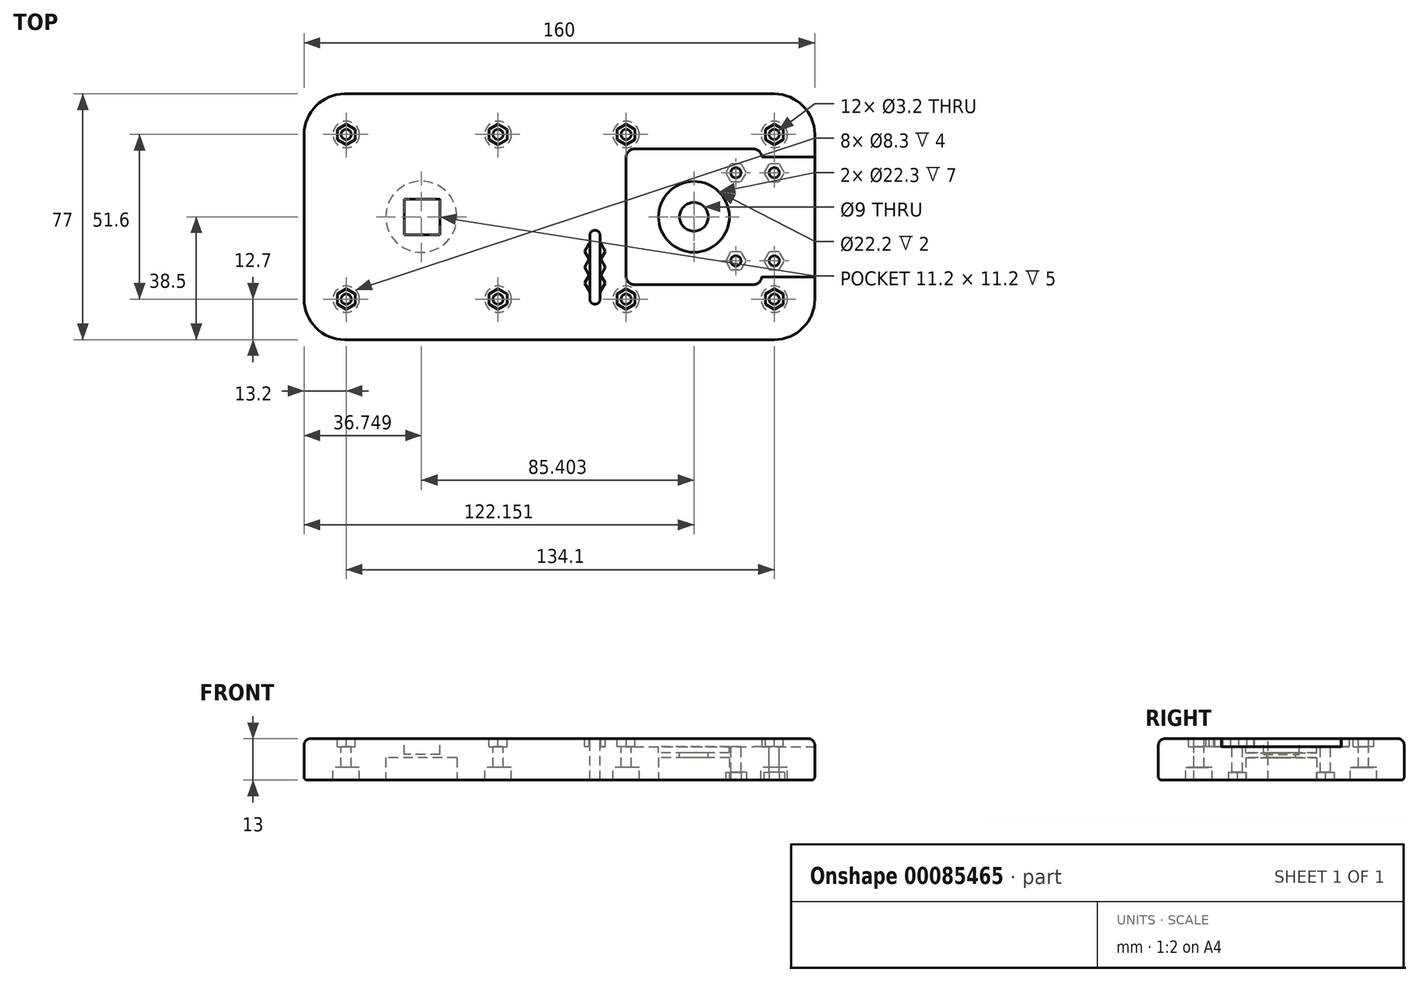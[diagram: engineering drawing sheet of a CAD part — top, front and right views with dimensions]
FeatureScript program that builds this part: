
annotation { "Feature Type Name" : "Feature", "Feature Type Description" : "" }
export const myFeature = defineFeature(function(context is Context, id is Id, definition is map)
    precondition{}
    {
        {
            var Q0;
            Q0=qCreatedBy(makeId("Top.planeOp"),FACE);
            var sketch = newSketch(context, id + "F0", { "sketchPlane" : qUnion([Q0])});
            skLineSegment(sketch, "E0.bottom", {"start": v(-147.3, 0) * mm, "end": v(-12.7, 0) * mm});
            skLineSegment(sketch, "E0.top", {"start": v(-147.3, 77) * mm, "end": v(-12.7, 77) * mm});
            skLineSegment(sketch, "E0.left", {"start": v(-160, 12.7) * mm, "end": v(-160, 64.3) * mm});
            skLineSegment(sketch, "E0.right", {"start": v(0, 12.7) * mm, "end": v(0, 64.3) * mm});
            skPoint(sketch, "E1.visualSharp", {"position": v(-160, 77) * mm});
            skArc(sketch, "E1.filletArc", {"start": v(-147.3, 77) * mm, "mid": v(-156.28, 73.28) * mm, "end": v(-160, 64.3) * mm});
            skPoint(sketch, "E2.visualSharp", {"position": v(0, 77) * mm});
            skArc(sketch, "E2.filletArc", {"start": v(0, 64.3) * mm, "mid": v(-3.72, 73.28) * mm, "end": v(-12.7, 77) * mm});
            skPoint(sketch, "E3.visualSharp", {"position": v(0, 0) * mm});
            skArc(sketch, "E3.filletArc", {"start": v(-12.7, 0) * mm, "mid": v(-3.72, 3.72) * mm, "end": v(0, 12.7) * mm});
            skPoint(sketch, "E4.visualSharp", {"position": v(-160, 0) * mm});
            skArc(sketch, "E4.filletArc", {"start": v(-160, 12.7) * mm, "mid": v(-156.28, 3.72) * mm, "end": v(-147.3, 0) * mm});
            skLineSegment(sketch, "E5.bottom", {"start": v(-56.56, 59.75) * mm, "end": v(-19.14, 59.75) * mm});
            skLineSegment(sketch, "E5.top", {"start": v(-56.56, 17.25) * mm, "end": v(-19.14, 17.25) * mm});
            skLineSegment(sketch, "E5.left", {"start": v(-59.1, 57.2) * mm, "end": v(-59.1, 19.79) * mm});
            skLineSegment(sketch, "E5.right", {"start": v(-16.6, 57.2) * mm, "end": v(-16.6, 19.79) * mm});
            skPoint(sketch, "E6.visualSharp", {"position": v(-59.1, 59.75) * mm});
            skArc(sketch, "E6.filletArc", {"start": v(-56.56, 59.75) * mm, "mid": v(-58.35, 59) * mm, "end": v(-59.1, 57.2) * mm});
            skPoint(sketch, "E7.visualSharp", {"position": v(-59.1, 17.25) * mm});
            skArc(sketch, "E7.filletArc", {"start": v(-59.1, 19.79) * mm, "mid": v(-58.35, 18) * mm, "end": v(-56.56, 17.25) * mm});
            skPoint(sketch, "E8.visualSharp", {"position": v(-16.6, 17.25) * mm});
            skArc(sketch, "E8.filletArc", {"start": v(-19.14, 17.25) * mm, "mid": v(-17.34, 18) * mm, "end": v(-16.6, 19.79) * mm});
            skPoint(sketch, "E9.visualSharp", {"position": v(-16.6, 59.75) * mm});
            skArc(sketch, "E9.filletArc", {"start": v(-16.6, 57.2) * mm, "mid": v(-17.34, 59) * mm, "end": v(-19.14, 59.75) * mm});
            skSolve(sketch);
        }
        {
            var Q0;
            Q0=makeQuery(id+"F0.imprint","IMPRINT",FACE,{"disambiguationData":[TD([[makeQuery(id+"F0.imprint","IMPRINT",EDGE,{"derivedFrom":sQuery(id+"F0.wireOp",EDGE,"E0.bottom")}),1.0]])]});
            extrude(context, id + "F1", {"entities" : qUnion([Q0]), "depth" : 13 * mm});
        }
        {
            var Q0;
            Q0=makeQuery(id+"F0.imprint","IMPRINT",FACE,{"disambiguationData":[TD([[makeQuery(id+"F0.imprint","IMPRINT",EDGE,{"derivedFrom":sQuery(id+"F0.wireOp",EDGE,"E5.bottom")}),-1.0]])]});
            extrude(context, id + "F2", {"entities" : qUnion([Q0]), "operationType" : NewBodyOperationType.ADD, "depth" : 10.5 * mm});
        }
        {
            var Q0;
            Q0=makeQuery(id+"F1.opExtrude","CAP_FACE",FACE,{"disambiguationData":[OSD([sQuery(id+"F0.wireOp",EDGE,"E0.bottom"),sQuery(id+"F0.wireOp",EDGE,"E0.top"),sQuery(id+"F0.wireOp",EDGE,"E0.left"),sQuery(id+"F0.wireOp",EDGE,"E0.right"),sQuery(id+"F0.wireOp",EDGE,"E1.filletArc"),sQuery(id+"F0.wireOp",EDGE,"E2.filletArc"),sQuery(id+"F0.wireOp",EDGE,"E3.filletArc"),sQuery(id+"F0.wireOp",EDGE,"E4.filletArc"),sQuery(id+"F0.wireOp",EDGE,"E5.bottom"),sQuery(id+"F0.wireOp",EDGE,"E5.top"),sQuery(id+"F0.wireOp",EDGE,"E5.left"),sQuery(id+"F0.wireOp",EDGE,"E5.right"),sQuery(id+"F0.wireOp",EDGE,"E6.filletArc"),sQuery(id+"F0.wireOp",EDGE,"E7.filletArc"),sQuery(id+"F0.wireOp",EDGE,"E8.filletArc"),sQuery(id+"F0.wireOp",EDGE,"E9.filletArc")])],"isStart":false});
            var sketch = newSketch(context, id + "F3", { "sketchPlane" : qUnion([Q0])});
            skLineSegment(sketch, "E10.right", {"start": v(-12.7, 64.3) * mm, "end": v(-12.7, 12.7) * mm, "construction": true});
            skCircle(sketch, "E11", {"center": v(-146.8, 64.3) * mm, "radius": 1.6 * mm});
            skCircle(sketch, "E12", {"center": v(-146.8, 12.7) * mm, "radius": 1.6 * mm});
            skCircle(sketch, "E13", {"center": v(-12.7, 12.7) * mm, "radius": 1.6 * mm});
            skCircle(sketch, "E14", {"center": v(-12.7, 64.3) * mm, "radius": 1.6 * mm});
            skCircle(sketch, "E15", {"center": v(-59.1, 12.7) * mm, "radius": 1.6 * mm});
            skCircle(sketch, "E16", {"center": v(-59.1, 64.3) * mm, "radius": 1.6 * mm});
            skCircle(sketch, "E17", {"center": v(-99.2, 64.3) * mm, "radius": 1.6 * mm});
            skCircle(sketch, "E18", {"center": v(-99.2, 12.7) * mm, "radius": 1.6 * mm});
            skCircle(sketch, "E19", {"center": v(-99.2, 64.3) * mm, "radius": 3 * mm});
            skCircle(sketch, "E20", {"center": v(-146.8, 64.3) * mm, "radius": 3 * mm});
            skCircle(sketch, "E21", {"center": v(-146.8, 12.7) * mm, "radius": 3 * mm});
            skCircle(sketch, "E22", {"center": v(-99.2, 12.7) * mm, "radius": 3 * mm});
            skLineSegment(sketch, "E23", {"start": v(-146.8, 12.7) * mm, "end": v(-12.7, 12.7) * mm, "construction": true});
            skLineSegment(sketch, "E24", {"start": v(-146.8, 64.3) * mm, "end": v(-12.7, 64.3) * mm, "construction": true});
            skLineSegment(sketch, "E25", {"start": v(-99.2, 64.3) * mm, "end": v(-99.2, 12.7) * mm, "construction": true});
            skLineSegment(sketch, "E26", {"start": v(-146.8, 12.7) * mm, "end": v(-146.8, 64.3) * mm, "construction": true});
            skLineSegment(sketch, "E27", {"start": v(-99.2, 12.7) * mm, "end": v(-146.8, 64.3) * mm, "construction": true});
            skLineSegment(sketch, "E28", {"start": v(-146.8, 12.7) * mm, "end": v(-99.2, 64.3) * mm, "construction": true});
            skCircle(sketch, "E29", {"center": v(-12.7, 64.3) * mm, "radius": 4.15 * mm});
            skCircle(sketch, "E30", {"center": v(-12.7, 12.7) * mm, "radius": 4.15 * mm});
            skCircle(sketch, "E31", {"center": v(-59.1, 12.7) * mm, "radius": 4.15 * mm});
            skCircle(sketch, "E32", {"center": v(-59.1, 64.3) * mm, "radius": 4.15 * mm});
            skCircle(sketch, "E33", {"center": v(-99.2, 64.3) * mm, "radius": 4.15 * mm});
            skCircle(sketch, "E34", {"center": v(-99.2, 12.7) * mm, "radius": 4.15 * mm});
            skCircle(sketch, "E35", {"center": v(-146.8, 12.7) * mm, "radius": 4.15 * mm});
            skCircle(sketch, "E36", {"center": v(-146.8, 64.3) * mm, "radius": 4.15 * mm});
            skLineSegment(sketch, "E37", {"start": v(-12.7, 64.3) * mm, "end": v(-12.7, 52.3) * mm, "construction": true});
            skLineSegment(sketch, "E38", {"start": v(-12.7, 12.7) * mm, "end": v(-12.7, 24.7) * mm, "construction": true});
            skLineSegment(sketch, "E39", {"start": v(-12.7, 24.7) * mm, "end": v(-24.7, 24.7) * mm, "construction": true});
            skLineSegment(sketch, "E40", {"start": v(-12.7, 52.3) * mm, "end": v(-24.7, 52.3) * mm, "construction": true});
            skCircle(sketch, "E41", {"center": v(-24.7, 52.3) * mm, "radius": 1.6 * mm});
            skCircle(sketch, "E42", {"center": v(-12.7, 52.3) * mm, "radius": 1.6 * mm});
            skCircle(sketch, "E43", {"center": v(-12.7, 24.7) * mm, "radius": 1.6 * mm});
            skCircle(sketch, "E44", {"center": v(-24.7, 24.7) * mm, "radius": 1.6 * mm});
            skPoint(sketch, "E45", {"position": v(-143.99, 15.75) * mm});
            skPoint(sketch, "E46", {"position": v(-102.02, 61.25) * mm});
            skSolve(sketch);
        }
        {
            var Q0;
            Q0=makeQuery(id+"F3.imprint","IMPRINT",FACE,{"disambiguationData":[TD([[makeQuery(id+"F3.imprint","IMPRINT",EDGE,{"derivedFrom":sQuery(id+"F3.wireOp",EDGE,"E11")}),1.0]])]});
            var Q1;
            Q1=makeQuery(id+"F3.imprint","IMPRINT",FACE,{"disambiguationData":[TD([[makeQuery(id+"F3.imprint","IMPRINT",EDGE,{"derivedFrom":sQuery(id+"F3.wireOp",EDGE,"E12")}),1.0]])]});
            var Q2;
            Q2=makeQuery(id+"F3.imprint","IMPRINT",FACE,{"disambiguationData":[TD([[makeQuery(id+"F3.imprint","IMPRINT",EDGE,{"derivedFrom":sQuery(id+"F3.wireOp",EDGE,"E13")}),1.0]])]});
            var Q3;
            Q3=makeQuery(id+"F3.imprint","IMPRINT",FACE,{"disambiguationData":[TD([[makeQuery(id+"F3.imprint","IMPRINT",EDGE,{"derivedFrom":sQuery(id+"F3.wireOp",EDGE,"E14")}),1.0]])]});
            var Q4;
            Q4=makeQuery(id+"F3.imprint","IMPRINT",FACE,{"disambiguationData":[TD([[makeQuery(id+"F3.imprint","IMPRINT",EDGE,{"derivedFrom":sQuery(id+"F3.wireOp",EDGE,"E15")}),1.0]])]});
            var Q5;
            Q5=makeQuery(id+"F3.imprint","IMPRINT",FACE,{"disambiguationData":[TD([[makeQuery(id+"F3.imprint","IMPRINT",EDGE,{"derivedFrom":sQuery(id+"F3.wireOp",EDGE,"E16")}),1.0]])]});
            var Q6;
            Q6=makeQuery(id+"F3.imprint","IMPRINT",FACE,{"disambiguationData":[TD([[makeQuery(id+"F3.imprint","IMPRINT",EDGE,{"derivedFrom":sQuery(id+"F3.wireOp",EDGE,"E17")}),1.0]])]});
            var Q7;
            Q7=makeQuery(id+"F3.imprint","IMPRINT",FACE,{"disambiguationData":[TD([[makeQuery(id+"F3.imprint","IMPRINT",EDGE,{"derivedFrom":sQuery(id+"F3.wireOp",EDGE,"E18")}),1.0]])]});
            var Q8;
            Q8=makeQuery(id+"F3.imprint","IMPRINT",FACE,{"disambiguationData":[TD([[makeQuery(id+"F3.imprint","IMPRINT",EDGE,{"derivedFrom":sQuery(id+"F3.wireOp",EDGE,"E42")}),1.0]])]});
            var Q9;
            Q9=makeQuery(id+"F3.imprint","IMPRINT",FACE,{"disambiguationData":[TD([[makeQuery(id+"F3.imprint","IMPRINT",EDGE,{"derivedFrom":sQuery(id+"F3.wireOp",EDGE,"E43")}),1.0]])]});
            var Q10;
            Q10=makeQuery(id+"F3.imprint","IMPRINT",FACE,{"disambiguationData":[TD([[makeQuery(id+"F3.imprint","IMPRINT",EDGE,{"derivedFrom":sQuery(id+"F3.wireOp",EDGE,"E44")}),1.0]])]});
            var Q11;
            Q11=makeQuery(id+"F3.imprint","IMPRINT",FACE,{"disambiguationData":[TD([[makeQuery(id+"F3.imprint","IMPRINT",EDGE,{"derivedFrom":sQuery(id+"F3.wireOp",EDGE,"E41")}),1.0]])]});
            extrude(context, id + "F4", {"entities" : qUnion([Q0, Q1, Q2, Q3, Q4, Q5, Q6, Q7, Q8, Q9, Q10, Q11]), "operationType" : NewBodyOperationType.REMOVE, "endBound" : BoundingType.UP_TO_NEXT, "oppositeDirection" : true, "depth" : 29.76 * mm});
        }
        {
            var Q0;
            Q0=makeQuery(id+"F0.imprint","IMPRINT",FACE,{"disambiguationData":[TD([[makeQuery(id+"F0.imprint","IMPRINT",EDGE,{"derivedFrom":sQuery(id+"F0.wireOp",EDGE,"E5.bottom")}),-1.0]])]});
            var sketch = newSketch(context, id + "F5", { "sketchPlane" : qUnion([Q0])});
            skLineSegment(sketch, "E47.0.0", {"start": v(-19.14, 59.75) * mm, "end": v(-56.56, 59.75) * mm});
            skArc(sketch, "E47.0.1", {"start": v(-56.56, 59.75) * mm, "mid": v(-58.35, 59) * mm, "end": v(-59.1, 57.2) * mm});
            skLineSegment(sketch, "E47.0.2", {"start": v(-59.1, 57.2) * mm, "end": v(-59.1, 19.79) * mm, "construction": true});
            skArc(sketch, "E47.0.3", {"start": v(-59.1, 19.79) * mm, "mid": v(-58.35, 18) * mm, "end": v(-56.56, 17.25) * mm, "construction": true});
            skLineSegment(sketch, "E47.0.4", {"start": v(-56.56, 17.25) * mm, "end": v(-19.14, 17.25) * mm});
            skArc(sketch, "E47.0.5", {"start": v(-19.14, 17.25) * mm, "mid": v(-17.34, 18) * mm, "end": v(-16.6, 19.79) * mm, "construction": true});
            skLineSegment(sketch, "E47.0.6", {"start": v(-16.6, 19.79) * mm, "end": v(-16.6, 57.2) * mm});
            skArc(sketch, "E47.0.7", {"start": v(-16.6, 57.2) * mm, "mid": v(-17.34, 59) * mm, "end": v(-19.14, 59.75) * mm, "construction": true});
            skLineSegment(sketch, "E48", {"start": v(-19.14, 19.79) * mm, "end": v(-56.56, 57.21) * mm, "construction": true});
            skLineSegment(sketch, "E49", {"start": v(-56.56, 19.79) * mm, "end": v(-19.14, 57.2) * mm, "construction": true});
            skPoint(sketch, "E50", {"position": v(-37.85, 38.5) * mm});
            skCircle(sketch, "E51", {"center": v(-37.85, 38.5) * mm, "radius": 11.15 * mm});
            skSolve(sketch);
        }
        {
            var Q0;
            Q0=qSketchRegion(id+"F5",true);
            extrude(context, id + "F6", {"entities" : qUnion([Q0]), "operationType" : NewBodyOperationType.REMOVE, "depth" : 7 * mm});
        }
        {
            var Q0;
            Q0=makeQuery(id+"F2.opExtrude","CAP_FACE",FACE,{"disambiguationData":[OSD([sQuery(id+"F0.wireOp",EDGE,"E5.bottom"),sQuery(id+"F0.wireOp",EDGE,"E5.top"),sQuery(id+"F0.wireOp",EDGE,"E5.left"),sQuery(id+"F0.wireOp",EDGE,"E5.right"),sQuery(id+"F0.wireOp",EDGE,"E6.filletArc"),sQuery(id+"F0.wireOp",EDGE,"E7.filletArc"),sQuery(id+"F0.wireOp",EDGE,"E8.filletArc"),sQuery(id+"F0.wireOp",EDGE,"E9.filletArc")])],"isStart":false});
            var sketch = newSketch(context, id + "F7", { "sketchPlane" : qUnion([Q0])});
            skLineSegment(sketch, "E52", {"start": v(-56.56, 19.79) * mm, "end": v(-19.14, 57.2) * mm, "construction": true});
            skLineSegment(sketch, "E53", {"start": v(-56.56, 57.21) * mm, "end": v(-19.14, 19.79) * mm, "construction": true});
            skCircle(sketch, "E54", {"center": v(-37.85, 38.5) * mm, "radius": 4.5 * mm});
            skCircle(sketch, "E55", {"center": v(-37.85, 38.5) * mm, "radius": 11.1 * mm});
            skSolve(sketch);
        }
        {
            var Q0;
            Q0=makeQuery(id+"F7.imprint","IMPRINT",FACE,{"disambiguationData":[TD([[makeQuery(id+"F7.imprint","IMPRINT",EDGE,{"derivedFrom":sQuery(id+"F7.wireOp",EDGE,"E54")}),1.0]])]});
            var Q1;
            Q1=sQuery(id+"F7.wireOp",EDGE,"E54");
            extrude(context, id + "F8", {"entities" : qUnion([Q0]), "operationType" : NewBodyOperationType.REMOVE, "surfaceEntities" : qUnion([Q1]), "oppositeDirection" : true, "depth" : 9 * mm});
        }
        {
            var Q0;
            Q0=makeQuery(id+"F0.imprint","IMPRINT",FACE,{"disambiguationData":[TD([[makeQuery(id+"F0.imprint","IMPRINT",EDGE,{"derivedFrom":sQuery(id+"F0.wireOp",EDGE,"E0.bottom")}),1.0]])]});
            var sketch = newSketch(context, id + "F9", { "sketchPlane" : qUnion([Q0])});
            skPoint(sketch, "E56.0", {"position": v(-147.3, 64.3) * mm});
            skCircle(sketch, "E57.0", {"center": v(-146.8, 64.3) * mm, "radius": 1.6 * mm});
            skCircle(sketch, "E58.0", {"center": v(-99.2, 64.3) * mm, "radius": 1.6 * mm});
            skCircle(sketch, "E59.0", {"center": v(-99.2, 12.7) * mm, "radius": 1.6 * mm});
            skCircle(sketch, "E60.0", {"center": v(-146.8, 12.7) * mm, "radius": 1.6 * mm});
            skLineSegment(sketch, "E61", {"start": v(-146.8, 12.7) * mm, "end": v(-99.2, 64.3) * mm, "construction": true});
            skLineSegment(sketch, "E62", {"start": v(-99.2, 12.7) * mm, "end": v(-147.3, 64.3) * mm, "construction": true});
            skPoint(sketch, "E63.endSnap0", {"position": v(-123.25, 38.5) * mm});
            skCircle(sketch, "E64.0", {"center": v(-59.1, 64.3) * mm, "radius": 1.6 * mm});
            skCircle(sketch, "E65.0", {"center": v(-12.7, 12.7) * mm, "radius": 1.6 * mm});
            skCircle(sketch, "E66.0", {"center": v(-12.7, 64.3) * mm, "radius": 1.6 * mm});
            skCircle(sketch, "E67.0", {"center": v(-59.1, 12.7) * mm, "radius": 1.6 * mm});
            skCircle(sketch, "E68.0", {"center": v(-37.85, 38.5) * mm, "radius": 4.5 * mm});
            skLineSegment(sketch, "E69", {"start": v(-123.25, 38.5) * mm, "end": v(-37.85, 38.5) * mm, "construction": true});
            skCircle(sketch, "E70", {"center": v(-123.25, 38.5) * mm, "radius": 11.15 * mm});
            skLineSegment(sketch, "E71", {"start": v(-146.8, 12.7) * mm, "end": v(-99.2, 12.7) * mm, "construction": true});
            skLineSegment(sketch, "E72", {"start": v(-59.1, 12.7) * mm, "end": v(-12.7, 12.7) * mm, "construction": true});
            skLineSegment(sketch, "E73", {"start": v(-123.25, 38.5) * mm, "end": v(-123.25, 12.7) * mm, "construction": true});
            skLineSegment(sketch, "E74", {"start": v(-37.85, 38.5) * mm, "end": v(-37.85, 12.7) * mm, "construction": true});
            skLineSegment(sketch, "E75", {"start": v(-123.25, 27.35) * mm, "end": v(-37.85, 27.35) * mm, "construction": true});
            skLineSegment(sketch, "E76.bottom", {"start": v(-67.85, 12.7) * mm, "end": v(-69.85, 12.7) * mm});
            skLineSegment(sketch, "E77", {"start": v(-68.85, 12.7) * mm, "end": v(-68.85, 17.7) * mm, "construction": true});
            skLineSegment(sketch, "E78", {"start": v(-68.85, 17.7) * mm, "end": v(-68.85, 22.7) * mm, "construction": true});
            skLineSegment(sketch, "E79", {"start": v(-68.85, 22.7) * mm, "end": v(-68.85, 27.7) * mm, "construction": true});
            skLineSegment(sketch, "E80", {"start": v(-68.85, 27.7) * mm, "end": v(-68.85, 32.7) * mm, "construction": true});
            skLineSegment(sketch, "E81", {"start": v(-69.85, 12.7) * mm, "end": v(-69.85, 32.7) * mm});
            skLineSegment(sketch, "E82", {"start": v(-69.85, 32.7) * mm, "end": v(-67.85, 32.7) * mm});
            skLineSegment(sketch, "E83", {"start": v(-67.85, 32.7) * mm, "end": v(-67.85, 12.7) * mm});
            skLineSegment(sketch, "E84", {"start": v(-37.85, 24.21) * mm, "end": v(-68.85, 24.21) * mm, "construction": true});
            skLineSegment(sketch, "E85", {"start": v(-68.52, 38.5) * mm, "end": v(-68.52, 32.7) * mm, "construction": true});
            skLineSegment(sketch, "E86", {"start": v(-59.1, 12.7) * mm, "end": v(-99.2, 12.7) * mm, "construction": true});
            skCircle(sketch, "E87.cCircle", {"center": v(-68.85, 32.7) * mm, "radius": 3.23 * mm, "construction": true});
            skLineSegment(sketch, "E87.0", {"start": v(-65.62, 32.7) * mm, "end": v(-67.23, 29.9) * mm});
            skLineSegment(sketch, "E87.1", {"start": v(-67.23, 29.9) * mm, "end": v(-70.47, 29.9) * mm});
            skLineSegment(sketch, "E87.2", {"start": v(-70.47, 29.9) * mm, "end": v(-72.08, 32.7) * mm});
            skLineSegment(sketch, "E87.3", {"start": v(-72.08, 32.7) * mm, "end": v(-70.47, 35.5) * mm});
            skLineSegment(sketch, "E87.4", {"start": v(-70.47, 35.5) * mm, "end": v(-67.23, 35.5) * mm});
            skLineSegment(sketch, "E87.5", {"start": v(-67.23, 35.5) * mm, "end": v(-65.62, 32.7) * mm});
            skCircle(sketch, "E88.cCircle", {"center": v(-68.85, 27.7) * mm, "radius": 3.23 * mm, "construction": true});
            skLineSegment(sketch, "E88.0", {"start": v(-65.62, 27.7) * mm, "end": v(-67.23, 24.9) * mm});
            skLineSegment(sketch, "E88.1", {"start": v(-67.23, 24.9) * mm, "end": v(-70.47, 24.9) * mm});
            skLineSegment(sketch, "E88.2", {"start": v(-70.47, 24.9) * mm, "end": v(-72.08, 27.7) * mm});
            skLineSegment(sketch, "E88.3", {"start": v(-72.08, 27.7) * mm, "end": v(-70.47, 30.5) * mm});
            skLineSegment(sketch, "E88.4", {"start": v(-70.47, 30.5) * mm, "end": v(-67.23, 30.5) * mm});
            skLineSegment(sketch, "E88.5", {"start": v(-67.23, 30.5) * mm, "end": v(-65.62, 27.7) * mm});
            skCircle(sketch, "E89.cCircle", {"center": v(-68.85, 22.7) * mm, "radius": 3.23 * mm, "construction": true});
            skLineSegment(sketch, "E89.0", {"start": v(-65.62, 22.7) * mm, "end": v(-67.23, 19.9) * mm});
            skLineSegment(sketch, "E89.1", {"start": v(-67.23, 19.9) * mm, "end": v(-70.47, 19.9) * mm});
            skLineSegment(sketch, "E89.2", {"start": v(-70.47, 19.9) * mm, "end": v(-72.08, 22.7) * mm});
            skLineSegment(sketch, "E89.3", {"start": v(-72.08, 22.7) * mm, "end": v(-70.47, 25.5) * mm});
            skLineSegment(sketch, "E89.4", {"start": v(-70.47, 25.5) * mm, "end": v(-67.23, 25.5) * mm});
            skLineSegment(sketch, "E89.5", {"start": v(-67.23, 25.5) * mm, "end": v(-65.62, 22.7) * mm});
            skCircle(sketch, "E90.cCircle", {"center": v(-68.85, 17.7) * mm, "radius": 3.23 * mm, "construction": true});
            skLineSegment(sketch, "E90.0", {"start": v(-65.62, 17.7) * mm, "end": v(-67.23, 14.9) * mm});
            skLineSegment(sketch, "E90.1", {"start": v(-67.23, 14.9) * mm, "end": v(-70.47, 14.9) * mm});
            skLineSegment(sketch, "E90.2", {"start": v(-70.47, 14.9) * mm, "end": v(-72.08, 17.7) * mm});
            skLineSegment(sketch, "E90.3", {"start": v(-72.08, 17.7) * mm, "end": v(-70.47, 20.5) * mm});
            skLineSegment(sketch, "E90.4", {"start": v(-70.47, 20.5) * mm, "end": v(-67.23, 20.5) * mm});
            skLineSegment(sketch, "E90.5", {"start": v(-67.23, 20.5) * mm, "end": v(-65.62, 17.7) * mm});
            skCircle(sketch, "E91.cCircle", {"center": v(-68.85, 12.7) * mm, "radius": 3.23 * mm, "construction": true});
            skLineSegment(sketch, "E91.0", {"start": v(-65.62, 12.7) * mm, "end": v(-67.23, 9.9) * mm});
            skLineSegment(sketch, "E91.1", {"start": v(-67.23, 9.9) * mm, "end": v(-70.47, 9.9) * mm});
            skLineSegment(sketch, "E91.2", {"start": v(-70.47, 9.9) * mm, "end": v(-72.08, 12.7) * mm});
            skLineSegment(sketch, "E91.3", {"start": v(-72.08, 12.7) * mm, "end": v(-70.47, 15.5) * mm});
            skLineSegment(sketch, "E91.4", {"start": v(-70.47, 15.5) * mm, "end": v(-67.23, 15.5) * mm});
            skLineSegment(sketch, "E91.5", {"start": v(-67.23, 15.5) * mm, "end": v(-65.62, 12.7) * mm});
            skSolve(sketch);
        }
        {
            var Q0;
            Q0=makeQuery(id+"F9.imprint","IMPRINT",FACE,{"disambiguationData":[TD([[makeQuery(id+"F9.imprint","IMPRINT",EDGE,{"derivedFrom":sQuery(id+"F9.wireOp",EDGE,"E70")}),1.0]])]});
            extrude(context, id + "F10", {"entities" : qUnion([Q0]), "operationType" : NewBodyOperationType.REMOVE, "depth" : 7 * mm});
        }
        {
            var Q0;
            Q0=makeQuery(id+"F3.imprint","IMPRINT",FACE,{"disambiguationData":[TD([[makeQuery(id+"F3.imprint","IMPRINT",EDGE,{"derivedFrom":sQuery(id+"F3.wireOp",EDGE,"E13")}),-1.0]])]});
            var Q1;
            Q1=makeQuery(id+"F3.imprint","IMPRINT",FACE,{"disambiguationData":[TD([[makeQuery(id+"F3.imprint","IMPRINT",EDGE,{"derivedFrom":sQuery(id+"F3.wireOp",EDGE,"E15")}),-1.0]])]});
            var Q2;
            Q2=makeQuery(id+"F3.imprint","IMPRINT",FACE,{"disambiguationData":[TD([[makeQuery(id+"F3.imprint","IMPRINT",EDGE,{"derivedFrom":sQuery(id+"F3.wireOp",EDGE,"E14")}),-1.0]])]});
            var Q3;
            Q3=makeQuery(id+"F3.imprint","IMPRINT",FACE,{"disambiguationData":[TD([[makeQuery(id+"F3.imprint","IMPRINT",EDGE,{"derivedFrom":sQuery(id+"F3.wireOp",EDGE,"E16")}),-1.0]])]});
            var Q4;
            Q4=makeQuery(id+"F3.imprint","IMPRINT",FACE,{"disambiguationData":[TD([[makeQuery(id+"F3.imprint","IMPRINT",EDGE,{"derivedFrom":sQuery(id+"F3.wireOp",EDGE,"E18")}),-1.0]])]});
            var Q5;
            Q5=makeQuery(id+"F3.imprint","IMPRINT",FACE,{"disambiguationData":[TD([[makeQuery(id+"F3.imprint","IMPRINT",EDGE,{"derivedFrom":sQuery(id+"F3.wireOp",EDGE,"E17")}),-1.0]])]});
            var Q6;
            Q6=makeQuery(id+"F3.imprint","IMPRINT",FACE,{"disambiguationData":[TD([[makeQuery(id+"F3.imprint","IMPRINT",EDGE,{"derivedFrom":sQuery(id+"F3.wireOp",EDGE,"E11")}),-1.0]])]});
            var Q7;
            Q7=makeQuery(id+"F3.imprint","IMPRINT",FACE,{"disambiguationData":[TD([[makeQuery(id+"F3.imprint","IMPRINT",EDGE,{"derivedFrom":sQuery(id+"F3.wireOp",EDGE,"E12")}),-1.0]])]});
            var Q8;
            {var subQ0=sQuery(id+"F3.wireOp",EDGE,"Ve5UWHnS-peIv-7Eyy-3Cd5-ivY1OEfJHqwA.left");var subQ1=sQuery(id+"F3.wireOp",EDGE,"Ve5UWHnS-peIv-7Eyy-3Cd5-ivY1OEfJHqwA.top");var subQ2=makeQuery(id+"F3.imprint","INTERSECT",VERTEX,{"derivedFrom":[subQ1,subQ0]});Q8=makeQuery(id+"F3.imprint","IMPRINT",FACE,{"disambiguationData":[TD([[makeQuery(id+"F3.imprint","IMPRINT",EDGE,{"disambiguationData":[TD([[subQ2,-1.0]])],"derivedFrom":subQ1}),1.0]])]});}
            var Q9;
            {var subQ0=sQuery(id+"F3.wireOp",EDGE,"Ve5UWHnS-peIv-7Eyy-3Cd5-ivY1OEfJHqwA.left");var subQ1=sQuery(id+"F3.wireOp",EDGE,"Ve5UWHnS-peIv-7Eyy-3Cd5-ivY1OEfJHqwA.bottom");var subQ2=makeQuery(id+"F3.imprint","INTERSECT",VERTEX,{"derivedFrom":[subQ1,subQ0]});Q9=makeQuery(id+"F3.imprint","IMPRINT",FACE,{"disambiguationData":[TD([[makeQuery(id+"F3.imprint","IMPRINT",EDGE,{"disambiguationData":[TD([[subQ2,-1.0]])],"derivedFrom":subQ1}),-1.0]])]});}
            var Q10;
            {var subQ0=sQuery(id+"F3.wireOp",EDGE,"qpdfHU9s-RBNK-oNWM-wD5O-6DZd83lqHaN6.left");var subQ1=sQuery(id+"F3.wireOp",EDGE,"qpdfHU9s-RBNK-oNWM-wD5O-6DZd83lqHaN6.top");var subQ2=makeQuery(id+"F3.imprint","INTERSECT",VERTEX,{"derivedFrom":[subQ1,subQ0]});Q10=makeQuery(id+"F3.imprint","IMPRINT",FACE,{"disambiguationData":[TD([[makeQuery(id+"F3.imprint","IMPRINT",EDGE,{"disambiguationData":[TD([[subQ2,-1.0]])],"derivedFrom":subQ1}),-1.0]])]});}
            var Q11;
            {var subQ0=sQuery(id+"F3.wireOp",EDGE,"qpdfHU9s-RBNK-oNWM-wD5O-6DZd83lqHaN6.right");var subQ1=sQuery(id+"F3.wireOp",EDGE,"qpdfHU9s-RBNK-oNWM-wD5O-6DZd83lqHaN6.top");var subQ2=makeQuery(id+"F3.imprint","INTERSECT",VERTEX,{"derivedFrom":[subQ1,subQ0]});Q11=makeQuery(id+"F3.imprint","IMPRINT",FACE,{"disambiguationData":[TD([[makeQuery(id+"F3.imprint","IMPRINT",EDGE,{"disambiguationData":[TD([[subQ2,1.0]])],"derivedFrom":subQ1}),-1.0]])]});}
            var Q12;
            {var subQ0=sQuery(id+"F3.wireOp",EDGE,"qpdfHU9s-RBNK-oNWM-wD5O-6DZd83lqHaN6.right");var subQ1=sQuery(id+"F3.wireOp",EDGE,"qpdfHU9s-RBNK-oNWM-wD5O-6DZd83lqHaN6.bottom");var subQ2=makeQuery(id+"F3.imprint","INTERSECT",VERTEX,{"derivedFrom":[subQ1,subQ0]});Q12=makeQuery(id+"F3.imprint","IMPRINT",FACE,{"disambiguationData":[TD([[makeQuery(id+"F3.imprint","IMPRINT",EDGE,{"disambiguationData":[TD([[subQ2,1.0]])],"derivedFrom":subQ1}),1.0]])]});}
            var Q13;
            {var subQ0=sQuery(id+"F3.wireOp",EDGE,"qpdfHU9s-RBNK-oNWM-wD5O-6DZd83lqHaN6.left");var subQ1=sQuery(id+"F3.wireOp",EDGE,"qpdfHU9s-RBNK-oNWM-wD5O-6DZd83lqHaN6.bottom");var subQ2=makeQuery(id+"F3.imprint","INTERSECT",VERTEX,{"derivedFrom":[subQ1,subQ0]});Q13=makeQuery(id+"F3.imprint","IMPRINT",FACE,{"disambiguationData":[TD([[makeQuery(id+"F3.imprint","IMPRINT",EDGE,{"disambiguationData":[TD([[subQ2,-1.0]])],"derivedFrom":subQ1}),1.0]])]});}
            var Q14;
            {var subQ0=sQuery(id+"F3.wireOp",EDGE,"Ve5UWHnS-peIv-7Eyy-3Cd5-ivY1OEfJHqwA.right");var subQ1=sQuery(id+"F3.wireOp",EDGE,"Ve5UWHnS-peIv-7Eyy-3Cd5-ivY1OEfJHqwA.top");var subQ2=makeQuery(id+"F3.imprint","INTERSECT",VERTEX,{"derivedFrom":[subQ1,subQ0]});Q14=makeQuery(id+"F3.imprint","IMPRINT",FACE,{"disambiguationData":[TD([[makeQuery(id+"F3.imprint","IMPRINT",EDGE,{"disambiguationData":[TD([[subQ2,1.0]])],"derivedFrom":subQ1}),1.0]])]});}
            var Q15;
            {var subQ0=sQuery(id+"F3.wireOp",EDGE,"Ve5UWHnS-peIv-7Eyy-3Cd5-ivY1OEfJHqwA.right");var subQ1=sQuery(id+"F3.wireOp",EDGE,"Ve5UWHnS-peIv-7Eyy-3Cd5-ivY1OEfJHqwA.bottom");var subQ2=makeQuery(id+"F3.imprint","INTERSECT",VERTEX,{"derivedFrom":[subQ1,subQ0]});Q15=makeQuery(id+"F3.imprint","IMPRINT",FACE,{"disambiguationData":[TD([[makeQuery(id+"F3.imprint","IMPRINT",EDGE,{"disambiguationData":[TD([[subQ2,1.0]])],"derivedFrom":subQ1}),-1.0]])]});}
            var Q16;
            {var subQ0=sQuery(id+"F3.wireOp",EDGE,"M7g3rWNN-r2re-sdfs-xWe1-7BCIrnAAYx4U.left");var subQ1=sQuery(id+"F3.wireOp",EDGE,"M7g3rWNN-r2re-sdfs-xWe1-7BCIrnAAYx4U.bottom");var subQ2=makeQuery(id+"F3.imprint","INTERSECT",VERTEX,{"derivedFrom":[subQ1,subQ0]});Q16=makeQuery(id+"F3.imprint","IMPRINT",FACE,{"disambiguationData":[TD([[makeQuery(id+"F3.imprint","IMPRINT",EDGE,{"disambiguationData":[TD([[subQ2,-1.0]])],"derivedFrom":subQ1}),-1.0]])]});}
            var Q17;
            {var subQ0=sQuery(id+"F3.wireOp",EDGE,"M7g3rWNN-r2re-sdfs-xWe1-7BCIrnAAYx4U.right");var subQ1=sQuery(id+"F3.wireOp",EDGE,"M7g3rWNN-r2re-sdfs-xWe1-7BCIrnAAYx4U.bottom");var subQ2=makeQuery(id+"F3.imprint","INTERSECT",VERTEX,{"derivedFrom":[subQ1,subQ0]});Q17=makeQuery(id+"F3.imprint","IMPRINT",FACE,{"disambiguationData":[TD([[makeQuery(id+"F3.imprint","IMPRINT",EDGE,{"disambiguationData":[TD([[subQ2,1.0]])],"derivedFrom":subQ1}),-1.0]])]});}
            var Q18;
            {var subQ0=sQuery(id+"F3.wireOp",EDGE,"M7g3rWNN-r2re-sdfs-xWe1-7BCIrnAAYx4U.right");var subQ1=sQuery(id+"F3.wireOp",EDGE,"M7g3rWNN-r2re-sdfs-xWe1-7BCIrnAAYx4U.top");var subQ2=makeQuery(id+"F3.imprint","INTERSECT",VERTEX,{"derivedFrom":[subQ1,subQ0]});Q18=makeQuery(id+"F3.imprint","IMPRINT",FACE,{"disambiguationData":[TD([[makeQuery(id+"F3.imprint","IMPRINT",EDGE,{"disambiguationData":[TD([[subQ2,1.0]])],"derivedFrom":subQ1}),1.0]])]});}
            var Q19;
            {var subQ0=sQuery(id+"F3.wireOp",EDGE,"M7g3rWNN-r2re-sdfs-xWe1-7BCIrnAAYx4U.left");var subQ1=sQuery(id+"F3.wireOp",EDGE,"M7g3rWNN-r2re-sdfs-xWe1-7BCIrnAAYx4U.top");var subQ2=makeQuery(id+"F3.imprint","INTERSECT",VERTEX,{"derivedFrom":[subQ1,subQ0]});Q19=makeQuery(id+"F3.imprint","IMPRINT",FACE,{"disambiguationData":[TD([[makeQuery(id+"F3.imprint","IMPRINT",EDGE,{"disambiguationData":[TD([[subQ2,-1.0]])],"derivedFrom":subQ1}),1.0]])]});}
            var Q20;
            {var subQ0=sQuery(id+"F3.wireOp",EDGE,"LNkkHq0Q-swaF-4Tb0-GpIf-acqlaCuNdGQa.left");var subQ1=sQuery(id+"F3.wireOp",EDGE,"LNkkHq0Q-swaF-4Tb0-GpIf-acqlaCuNdGQa.bottom");var subQ2=makeQuery(id+"F3.imprint","INTERSECT",VERTEX,{"derivedFrom":[subQ1,subQ0]});Q20=makeQuery(id+"F3.imprint","IMPRINT",FACE,{"disambiguationData":[TD([[makeQuery(id+"F3.imprint","IMPRINT",EDGE,{"disambiguationData":[TD([[subQ2,-1.0]])],"derivedFrom":subQ1}),-1.0]])]});}
            var Q21;
            {var subQ0=sQuery(id+"F3.wireOp",EDGE,"LNkkHq0Q-swaF-4Tb0-GpIf-acqlaCuNdGQa.right");var subQ1=sQuery(id+"F3.wireOp",EDGE,"LNkkHq0Q-swaF-4Tb0-GpIf-acqlaCuNdGQa.bottom");var subQ2=makeQuery(id+"F3.imprint","INTERSECT",VERTEX,{"derivedFrom":[subQ1,subQ0]});Q21=makeQuery(id+"F3.imprint","IMPRINT",FACE,{"disambiguationData":[TD([[makeQuery(id+"F3.imprint","IMPRINT",EDGE,{"disambiguationData":[TD([[subQ2,1.0]])],"derivedFrom":subQ1}),-1.0]])]});}
            var Q22;
            {var subQ0=sQuery(id+"F3.wireOp",EDGE,"LNkkHq0Q-swaF-4Tb0-GpIf-acqlaCuNdGQa.right");var subQ1=sQuery(id+"F3.wireOp",EDGE,"LNkkHq0Q-swaF-4Tb0-GpIf-acqlaCuNdGQa.top");var subQ2=makeQuery(id+"F3.imprint","INTERSECT",VERTEX,{"derivedFrom":[subQ1,subQ0]});Q22=makeQuery(id+"F3.imprint","IMPRINT",FACE,{"disambiguationData":[TD([[makeQuery(id+"F3.imprint","IMPRINT",EDGE,{"disambiguationData":[TD([[subQ2,1.0]])],"derivedFrom":subQ1}),1.0]])]});}
            var Q23;
            {var subQ0=sQuery(id+"F3.wireOp",EDGE,"LNkkHq0Q-swaF-4Tb0-GpIf-acqlaCuNdGQa.left");var subQ1=sQuery(id+"F3.wireOp",EDGE,"LNkkHq0Q-swaF-4Tb0-GpIf-acqlaCuNdGQa.top");var subQ2=makeQuery(id+"F3.imprint","INTERSECT",VERTEX,{"derivedFrom":[subQ1,subQ0]});Q23=makeQuery(id+"F3.imprint","IMPRINT",FACE,{"disambiguationData":[TD([[makeQuery(id+"F3.imprint","IMPRINT",EDGE,{"disambiguationData":[TD([[subQ2,-1.0]])],"derivedFrom":subQ1}),1.0]])]});}
            var Q24;
            Q24=makeQuery(id+"F3.imprint","IMPRINT",FACE,{"disambiguationData":[TD([[makeQuery(id+"F3.imprint","IMPRINT",EDGE,{"derivedFrom":sQuery(id+"F3.wireOp",EDGE,"E36")}),1.0]])]});
            var Q25;
            {var subQ0=sQuery(id+"F3.wireOp",EDGE,"E20");var subQ1=sQuery(id+"F3.wireOp",EDGE,"Ve5UWHnS-peIv-7Eyy-3Cd5-ivY1OEfJHqwA.left");var subQ2=makeQuery(id+"F3.imprint","INTERSECT",VERTEX,{"disambiguationData":[OD(0.0)],"derivedFrom":[subQ1,subQ0]});Q25=makeQuery(id+"F3.imprint","IMPRINT",FACE,{"disambiguationData":[TD([[makeQuery(id+"F3.imprint","IMPRINT",EDGE,{"disambiguationData":[TD([[subQ2,-1.0]])],"derivedFrom":subQ1}),-1.0]])]});}
            var Q26;
            {var subQ0=sQuery(id+"F3.wireOp",EDGE,"E20");var subQ1=sQuery(id+"F3.wireOp",EDGE,"Ve5UWHnS-peIv-7Eyy-3Cd5-ivY1OEfJHqwA.top");var subQ2=makeQuery(id+"F3.imprint","INTERSECT",VERTEX,{"disambiguationData":[OD(0.0)],"derivedFrom":[subQ1,subQ0]});Q26=makeQuery(id+"F3.imprint","IMPRINT",FACE,{"disambiguationData":[TD([[makeQuery(id+"F3.imprint","IMPRINT",EDGE,{"disambiguationData":[TD([[subQ2,-1.0]])],"derivedFrom":subQ1}),-1.0]])]});}
            var Q27;
            {var subQ0=sQuery(id+"F3.wireOp",EDGE,"E20");var subQ1=sQuery(id+"F3.wireOp",EDGE,"Ve5UWHnS-peIv-7Eyy-3Cd5-ivY1OEfJHqwA.bottom");var subQ2=makeQuery(id+"F3.imprint","INTERSECT",VERTEX,{"disambiguationData":[OD(0.0)],"derivedFrom":[subQ1,subQ0]});Q27=makeQuery(id+"F3.imprint","IMPRINT",FACE,{"disambiguationData":[TD([[makeQuery(id+"F3.imprint","IMPRINT",EDGE,{"disambiguationData":[TD([[subQ2,-1.0]])],"derivedFrom":subQ1}),1.0]])]});}
            var Q28;
            {var subQ0=sQuery(id+"F3.wireOp",EDGE,"E20");var subQ1=sQuery(id+"F3.wireOp",EDGE,"Ve5UWHnS-peIv-7Eyy-3Cd5-ivY1OEfJHqwA.right");var subQ2=makeQuery(id+"F3.imprint","INTERSECT",VERTEX,{"disambiguationData":[OD(0.0)],"derivedFrom":[subQ1,subQ0]});Q28=makeQuery(id+"F3.imprint","IMPRINT",FACE,{"disambiguationData":[TD([[makeQuery(id+"F3.imprint","IMPRINT",EDGE,{"disambiguationData":[TD([[subQ2,-1.0]])],"derivedFrom":subQ1}),1.0]])]});}
            var Q29;
            {var subQ0=sQuery(id+"F3.wireOp",EDGE,"E19");var subQ1=sQuery(id+"F3.wireOp",EDGE,"qpdfHU9s-RBNK-oNWM-wD5O-6DZd83lqHaN6.top");var subQ2=makeQuery(id+"F3.imprint","INTERSECT",VERTEX,{"disambiguationData":[OD(0.0)],"derivedFrom":[subQ1,subQ0]});Q29=makeQuery(id+"F3.imprint","IMPRINT",FACE,{"disambiguationData":[TD([[makeQuery(id+"F3.imprint","IMPRINT",EDGE,{"disambiguationData":[TD([[subQ2,-1.0]])],"derivedFrom":subQ1}),1.0]])]});}
            var Q30;
            {var subQ0=sQuery(id+"F3.wireOp",EDGE,"E19");var subQ1=sQuery(id+"F3.wireOp",EDGE,"qpdfHU9s-RBNK-oNWM-wD5O-6DZd83lqHaN6.right");var subQ2=makeQuery(id+"F3.imprint","INTERSECT",VERTEX,{"disambiguationData":[OD(0.0)],"derivedFrom":[subQ1,subQ0]});Q30=makeQuery(id+"F3.imprint","IMPRINT",FACE,{"disambiguationData":[TD([[makeQuery(id+"F3.imprint","IMPRINT",EDGE,{"disambiguationData":[TD([[subQ2,-1.0]])],"derivedFrom":subQ1}),-1.0]])]});}
            var Q31;
            {var subQ0=sQuery(id+"F3.wireOp",EDGE,"E19");var subQ1=sQuery(id+"F3.wireOp",EDGE,"qpdfHU9s-RBNK-oNWM-wD5O-6DZd83lqHaN6.bottom");var subQ2=makeQuery(id+"F3.imprint","INTERSECT",VERTEX,{"disambiguationData":[OD(0.0)],"derivedFrom":[subQ1,subQ0]});Q31=makeQuery(id+"F3.imprint","IMPRINT",FACE,{"disambiguationData":[TD([[makeQuery(id+"F3.imprint","IMPRINT",EDGE,{"disambiguationData":[TD([[subQ2,-1.0]])],"derivedFrom":subQ1}),-1.0]])]});}
            var Q32;
            {var subQ0=sQuery(id+"F3.wireOp",EDGE,"E19");var subQ1=sQuery(id+"F3.wireOp",EDGE,"qpdfHU9s-RBNK-oNWM-wD5O-6DZd83lqHaN6.left");var subQ2=makeQuery(id+"F3.imprint","INTERSECT",VERTEX,{"disambiguationData":[OD(0.0)],"derivedFrom":[subQ1,subQ0]});Q32=makeQuery(id+"F3.imprint","IMPRINT",FACE,{"disambiguationData":[TD([[makeQuery(id+"F3.imprint","IMPRINT",EDGE,{"disambiguationData":[TD([[subQ2,-1.0]])],"derivedFrom":subQ1}),1.0]])]});}
            var Q33;
            {var subQ0=sQuery(id+"F3.wireOp",EDGE,"E22");var subQ1=sQuery(id+"F3.wireOp",EDGE,"LNkkHq0Q-swaF-4Tb0-GpIf-acqlaCuNdGQa.left");var subQ2=makeQuery(id+"F3.imprint","INTERSECT",VERTEX,{"disambiguationData":[OD(0.0)],"derivedFrom":[subQ1,subQ0]});Q33=makeQuery(id+"F3.imprint","IMPRINT",FACE,{"disambiguationData":[TD([[makeQuery(id+"F3.imprint","IMPRINT",EDGE,{"disambiguationData":[TD([[subQ2,-1.0]])],"derivedFrom":subQ1}),-1.0]])]});}
            var Q34;
            {var subQ0=sQuery(id+"F3.wireOp",EDGE,"E22");var subQ1=sQuery(id+"F3.wireOp",EDGE,"LNkkHq0Q-swaF-4Tb0-GpIf-acqlaCuNdGQa.top");var subQ2=makeQuery(id+"F3.imprint","INTERSECT",VERTEX,{"disambiguationData":[OD(0.0)],"derivedFrom":[subQ1,subQ0]});Q34=makeQuery(id+"F3.imprint","IMPRINT",FACE,{"disambiguationData":[TD([[makeQuery(id+"F3.imprint","IMPRINT",EDGE,{"disambiguationData":[TD([[subQ2,-1.0]])],"derivedFrom":subQ1}),-1.0]])]});}
            var Q35;
            {var subQ0=sQuery(id+"F3.wireOp",EDGE,"E22");var subQ1=sQuery(id+"F3.wireOp",EDGE,"LNkkHq0Q-swaF-4Tb0-GpIf-acqlaCuNdGQa.right");var subQ2=makeQuery(id+"F3.imprint","INTERSECT",VERTEX,{"disambiguationData":[OD(0.0)],"derivedFrom":[subQ1,subQ0]});Q35=makeQuery(id+"F3.imprint","IMPRINT",FACE,{"disambiguationData":[TD([[makeQuery(id+"F3.imprint","IMPRINT",EDGE,{"disambiguationData":[TD([[subQ2,-1.0]])],"derivedFrom":subQ1}),1.0]])]});}
            var Q36;
            {var subQ0=sQuery(id+"F3.wireOp",EDGE,"E22");var subQ1=sQuery(id+"F3.wireOp",EDGE,"LNkkHq0Q-swaF-4Tb0-GpIf-acqlaCuNdGQa.bottom");var subQ2=makeQuery(id+"F3.imprint","INTERSECT",VERTEX,{"disambiguationData":[OD(0.0)],"derivedFrom":[subQ1,subQ0]});Q36=makeQuery(id+"F3.imprint","IMPRINT",FACE,{"disambiguationData":[TD([[makeQuery(id+"F3.imprint","IMPRINT",EDGE,{"disambiguationData":[TD([[subQ2,-1.0]])],"derivedFrom":subQ1}),1.0]])]});}
            var Q37;
            Q37=makeQuery(id+"F3.imprint","IMPRINT",FACE,{"disambiguationData":[TD([[makeQuery(id+"F3.imprint","IMPRINT",EDGE,{"derivedFrom":sQuery(id+"F3.wireOp",EDGE,"E34")}),1.0]])]});
            var Q38;
            Q38=makeQuery(id+"F3.imprint","IMPRINT",FACE,{"disambiguationData":[TD([[makeQuery(id+"F3.imprint","IMPRINT",EDGE,{"derivedFrom":sQuery(id+"F3.wireOp",EDGE,"E33")}),1.0]])]});
            var Q39;
            Q39=makeQuery(id+"F3.imprint","IMPRINT",FACE,{"disambiguationData":[TD([[makeQuery(id+"F3.imprint","IMPRINT",EDGE,{"derivedFrom":sQuery(id+"F3.wireOp",EDGE,"bCsaOFDC-J4Tw-3jIP-NfPT-4Dm8dlOxar3i.bottom")}),1.0]])]});
            var Q40;
            {var subQ0=sQuery(id+"F3.wireOp",EDGE,"E31");var subQ1=makeQuery(id+"F1.opExtrude","CAP_EDGE",EDGE,{"disambiguationData":[OSD([sQuery(id+"F0.wireOp",EDGE,"E5.top")])],"isStart":false});var subQ2=makeQuery(id+"F3.imprint","INTERSECT",VERTEX,{"derivedFrom":[subQ1,subQ0]});Q40=makeQuery(id+"F3.imprint","IMPRINT",FACE,{"disambiguationData":[TD([[makeQuery(id+"F3.imprint","IMPRINT",EDGE,{"disambiguationData":[TD([[subQ2,-1.0]])],"derivedFrom":subQ0}),1.0]])]});}
            var Q41;
            Q41=makeQuery(id+"F3.imprint","IMPRINT",FACE,{"disambiguationData":[TD([[makeQuery(id+"F3.imprint","IMPRINT",EDGE,{"derivedFrom":sQuery(id+"F3.wireOp",EDGE,"KdmdXQ9W-tjxg-HIv8-NmZo-p2fYIrPSUl3x.bottom")}),1.0]])]});
            var Q42;
            {var subQ0=sQuery(id+"F3.wireOp",EDGE,"E32");var subQ1=makeQuery(id+"F1.opExtrude","CAP_EDGE",EDGE,{"disambiguationData":[OSD([sQuery(id+"F0.wireOp",EDGE,"E5.bottom")])],"isStart":false});var subQ2=makeQuery(id+"F3.imprint","INTERSECT",VERTEX,{"derivedFrom":[subQ1,subQ0]});Q42=makeQuery(id+"F3.imprint","IMPRINT",FACE,{"disambiguationData":[TD([[makeQuery(id+"F3.imprint","IMPRINT",EDGE,{"disambiguationData":[TD([[subQ2,1.0]])],"derivedFrom":subQ0}),1.0]])]});}
            var Q43;
            Q43=makeQuery(id+"F3.imprint","IMPRINT",FACE,{"disambiguationData":[TD([[makeQuery(id+"F3.imprint","IMPRINT",EDGE,{"derivedFrom":sQuery(id+"F3.wireOp",EDGE,"K4wHa3xG-MwQd-eDoG-XvLQ-k9tKwPybIGie.bottom")}),-1.0]])]});
            var Q44;
            Q44=makeQuery(id+"F3.imprint","IMPRINT",FACE,{"disambiguationData":[TD([[makeQuery(id+"F3.imprint","IMPRINT",EDGE,{"derivedFrom":sQuery(id+"F3.wireOp",EDGE,"9oEyg2Ok-q2jv-9wrR-BUKK-CIbaopgzIB1s.bottom")}),-1.0]])]});
            var Q45;
            Q45=makeQuery(id+"F3.imprint","IMPRINT",FACE,{"disambiguationData":[TD([[makeQuery(id+"F3.imprint","IMPRINT",EDGE,{"derivedFrom":sQuery(id+"F3.wireOp",EDGE,"E35")}),1.0]])]});
            var Q46;
            {var subQ0=sQuery(id+"F3.wireOp",EDGE,"E21");var subQ1=sQuery(id+"F3.wireOp",EDGE,"M7g3rWNN-r2re-sdfs-xWe1-7BCIrnAAYx4U.bottom");var subQ2=makeQuery(id+"F3.imprint","INTERSECT",VERTEX,{"disambiguationData":[OD(0.0)],"derivedFrom":[subQ1,subQ0]});Q46=makeQuery(id+"F3.imprint","IMPRINT",FACE,{"disambiguationData":[TD([[makeQuery(id+"F3.imprint","IMPRINT",EDGE,{"disambiguationData":[TD([[subQ2,-1.0]])],"derivedFrom":subQ1}),1.0]])]});}
            var Q47;
            {var subQ0=sQuery(id+"F3.wireOp",EDGE,"E21");var subQ1=sQuery(id+"F3.wireOp",EDGE,"M7g3rWNN-r2re-sdfs-xWe1-7BCIrnAAYx4U.left");var subQ2=makeQuery(id+"F3.imprint","INTERSECT",VERTEX,{"disambiguationData":[OD(0.0)],"derivedFrom":[subQ1,subQ0]});Q47=makeQuery(id+"F3.imprint","IMPRINT",FACE,{"disambiguationData":[TD([[makeQuery(id+"F3.imprint","IMPRINT",EDGE,{"disambiguationData":[TD([[subQ2,-1.0]])],"derivedFrom":subQ1}),-1.0]])]});}
            var Q48;
            {var subQ0=sQuery(id+"F3.wireOp",EDGE,"E21");var subQ1=sQuery(id+"F3.wireOp",EDGE,"M7g3rWNN-r2re-sdfs-xWe1-7BCIrnAAYx4U.top");var subQ2=makeQuery(id+"F3.imprint","INTERSECT",VERTEX,{"disambiguationData":[OD(0.0)],"derivedFrom":[subQ1,subQ0]});Q48=makeQuery(id+"F3.imprint","IMPRINT",FACE,{"disambiguationData":[TD([[makeQuery(id+"F3.imprint","IMPRINT",EDGE,{"disambiguationData":[TD([[subQ2,-1.0]])],"derivedFrom":subQ1}),-1.0]])]});}
            var Q49;
            {var subQ0=sQuery(id+"F3.wireOp",EDGE,"E21");var subQ1=sQuery(id+"F3.wireOp",EDGE,"M7g3rWNN-r2re-sdfs-xWe1-7BCIrnAAYx4U.right");var subQ2=makeQuery(id+"F3.imprint","INTERSECT",VERTEX,{"disambiguationData":[OD(0.0)],"derivedFrom":[subQ1,subQ0]});Q49=makeQuery(id+"F3.imprint","IMPRINT",FACE,{"disambiguationData":[TD([[makeQuery(id+"F3.imprint","IMPRINT",EDGE,{"disambiguationData":[TD([[subQ2,-1.0]])],"derivedFrom":subQ1}),1.0]])]});}
            var Q50;
            {var subQ0=sQuery(id+"F0.wireOp",EDGE,"E9.filletArc");var subQ1=sQuery(id+"F0.wireOp",EDGE,"E8.filletArc");var subQ2=sQuery(id+"F0.wireOp",EDGE,"E7.filletArc");var subQ3=sQuery(id+"F0.wireOp",EDGE,"E6.filletArc");var subQ4=sQuery(id+"F0.wireOp",EDGE,"E5.right");var subQ5=sQuery(id+"F0.wireOp",EDGE,"E5.left");var subQ6=sQuery(id+"F0.wireOp",EDGE,"E5.top");var subQ7=sQuery(id+"F0.wireOp",EDGE,"E5.bottom");Q50=makeQuery(id+"F2.boolean.opBoolean","MERGE",FACE,{"derivedFrom":[makeQuery(id+"F1.opExtrude","CAP_FACE",FACE,{"disambiguationData":[OSD([sQuery(id+"F0.wireOp",EDGE,"E0.bottom"),sQuery(id+"F0.wireOp",EDGE,"E0.top"),sQuery(id+"F0.wireOp",EDGE,"E0.left"),sQuery(id+"F0.wireOp",EDGE,"E0.right"),sQuery(id+"F0.wireOp",EDGE,"E1.filletArc"),sQuery(id+"F0.wireOp",EDGE,"E2.filletArc"),sQuery(id+"F0.wireOp",EDGE,"E3.filletArc"),sQuery(id+"F0.wireOp",EDGE,"E4.filletArc"),subQ7,subQ6,subQ5,subQ4,subQ3,subQ2,subQ1,subQ0])],"isStart":true}),makeQuery(id+"F2.opExtrude","CAP_FACE",FACE,{"disambiguationData":[OSD([subQ7,subQ6,subQ5,subQ4,subQ3,subQ2,subQ1,subQ0])],"isStart":true})]});}
            extrude(context, id + "F11", {"entities" : qUnion([Q0, Q1, Q2, Q3, Q4, Q5, Q6, Q7, Q8, Q9, Q10, Q11, Q12, Q13, Q14, Q15, Q16, Q17, Q18, Q19, Q20, Q21, Q22, Q23, Q24, Q25, Q26, Q27, Q28, Q29, Q30, Q31, Q32, Q33, Q34, Q35, Q36, Q37, Q38, Q39, Q40, Q41, Q42, Q43, Q44, Q45, Q46, Q47, Q48, Q49]), "operationType" : NewBodyOperationType.REMOVE, "endBound" : BoundingType.UP_TO_SURFACE, "oppositeDirection" : true, "endBoundEntityFace" : qUnion([Q50]), "depth" : 18.58 * mm, "hasSecondDirection" : true, "secondDirectionOppositeDirection" : true, "secondDirectionDepth" : 9 * mm});
        }
        {
            var Q0;
            Q0=makeQuery(id+"F1.opExtrude","CAP_FACE",FACE,{"disambiguationData":[OSD([sQuery(id+"F0.wireOp",EDGE,"E0.bottom"),sQuery(id+"F0.wireOp",EDGE,"E0.top"),sQuery(id+"F0.wireOp",EDGE,"E0.left"),sQuery(id+"F0.wireOp",EDGE,"E0.right"),sQuery(id+"F0.wireOp",EDGE,"E1.filletArc"),sQuery(id+"F0.wireOp",EDGE,"E2.filletArc"),sQuery(id+"F0.wireOp",EDGE,"E3.filletArc"),sQuery(id+"F0.wireOp",EDGE,"E4.filletArc"),sQuery(id+"F0.wireOp",EDGE,"E5.bottom"),sQuery(id+"F0.wireOp",EDGE,"E5.top"),sQuery(id+"F0.wireOp",EDGE,"E5.left"),sQuery(id+"F0.wireOp",EDGE,"E5.right"),sQuery(id+"F0.wireOp",EDGE,"E6.filletArc"),sQuery(id+"F0.wireOp",EDGE,"E7.filletArc"),sQuery(id+"F0.wireOp",EDGE,"E8.filletArc"),sQuery(id+"F0.wireOp",EDGE,"E9.filletArc")])],"isStart":false});
            var sketch = newSketch(context, id + "F12", { "sketchPlane" : qUnion([Q0])});
            skLineSegment(sketch, "E92.bottom", {"start": v(-117.4, 32.9) * mm, "end": v(-128.6, 32.9) * mm});
            skLineSegment(sketch, "E92.top", {"start": v(-117.4, 44.1) * mm, "end": v(-128.6, 44.1) * mm});
            skLineSegment(sketch, "E92.left", {"start": v(-117.4, 32.9) * mm, "end": v(-117.4, 44.1) * mm});
            skLineSegment(sketch, "E92.right", {"start": v(-128.6, 32.9) * mm, "end": v(-128.6, 44.1) * mm});
            skLineSegment(sketch, "E93.top", {"start": v(-99.2, 64.3) * mm, "end": v(-146.8, 64.3) * mm, "construction": true});
            skLineSegment(sketch, "E93.right", {"start": v(-146.8, 12.7) * mm, "end": v(-146.8, 64.3) * mm, "construction": true});
            skPoint(sketch, "E94", {"position": v(-99.2, 12.7) * mm});
            skLineSegment(sketch, "E95", {"start": v(-146.8, 64.3) * mm, "end": v(-99.2, 12.7) * mm, "construction": true});
            skLineSegment(sketch, "E96", {"start": v(-99.2, 64.3) * mm, "end": v(-146.8, 12.7) * mm, "construction": true});
            skLineSegment(sketch, "E97", {"start": v(-128.6, 44.1) * mm, "end": v(-117.4, 32.9) * mm, "construction": true});
            skLineSegment(sketch, "E98", {"start": v(-117.4, 44.1) * mm, "end": v(-128.6, 32.9) * mm, "construction": true});
            skPoint(sketch, "E99", {"position": v(-123, 38.5) * mm});
            skLineSegment(sketch, "E100", {"start": v(-99.2, 64.3) * mm, "end": v(-99.2, 12.7) * mm, "construction": true});
            skLineSegment(sketch, "E101", {"start": v(-146.8, 12.7) * mm, "end": v(-99.2, 12.7) * mm, "construction": true});
            skSolve(sketch);
        }
        {
            var Q0;
            Q0=makeQuery(id+"F12.imprint","IMPRINT",FACE,{"disambiguationData":[TD([[makeQuery(id+"F12.imprint","IMPRINT",EDGE,{"derivedFrom":sQuery(id+"F12.wireOp",EDGE,"E92.bottom")}),-1.0]])]});
            extrude(context, id + "F13", {"entities" : qUnion([Q0]), "operationType" : NewBodyOperationType.REMOVE, "oppositeDirection" : true, "depth" : 5 * mm});
        }
        {
            var Q0;
            Q0=makeQuery(id+"F7.imprint","IMPRINT",FACE,{"disambiguationData":[TD([[makeQuery(id+"F7.imprint","IMPRINT",EDGE,{"derivedFrom":sQuery(id+"F7.wireOp",EDGE,"E54")}),-1.0]])]});
            extrude(context, id + "F14", {"entities" : qUnion([Q0]), "operationType" : NewBodyOperationType.REMOVE, "oppositeDirection" : true, "depth" : 2 * mm});
        }
        {
            var Q0;
            Q0=makeQuery(id+"F3.imprint","IMPRINT",FACE,{"disambiguationData":[TD([[makeQuery(id+"F3.imprint","IMPRINT",EDGE,{"derivedFrom":sQuery(id+"F3.wireOp",EDGE,"E41")}),1.0]])]});
            var Q1;
            Q1=makeQuery(id+"F3.imprint","IMPRINT",FACE,{"disambiguationData":[TD([[makeQuery(id+"F3.imprint","IMPRINT",EDGE,{"derivedFrom":sQuery(id+"F3.wireOp",EDGE,"E44")}),1.0]])]});
            extrude(context, id + "F15", {"entities" : qUnion([Q0, Q1]), "operationType" : NewBodyOperationType.REMOVE, "oppositeDirection" : true, "depth" : 25 * mm});
        }
        {
            var Q0;
            {var subQ0=sQuery(id+"F0.wireOp",EDGE,"E9.filletArc");var subQ1=sQuery(id+"F0.wireOp",EDGE,"E8.filletArc");var subQ2=sQuery(id+"F0.wireOp",EDGE,"E7.filletArc");var subQ3=sQuery(id+"F0.wireOp",EDGE,"E6.filletArc");var subQ4=sQuery(id+"F0.wireOp",EDGE,"E5.right");var subQ5=sQuery(id+"F0.wireOp",EDGE,"E5.left");var subQ6=sQuery(id+"F0.wireOp",EDGE,"E5.top");var subQ7=sQuery(id+"F0.wireOp",EDGE,"E5.bottom");Q0=makeQuery(id+"F2.boolean.opBoolean","MERGE",FACE,{"derivedFrom":[makeQuery(id+"F1.opExtrude","CAP_FACE",FACE,{"disambiguationData":[OSD([sQuery(id+"F0.wireOp",EDGE,"E0.bottom"),sQuery(id+"F0.wireOp",EDGE,"E0.top"),sQuery(id+"F0.wireOp",EDGE,"E0.left"),sQuery(id+"F0.wireOp",EDGE,"E0.right"),sQuery(id+"F0.wireOp",EDGE,"E1.filletArc"),sQuery(id+"F0.wireOp",EDGE,"E2.filletArc"),sQuery(id+"F0.wireOp",EDGE,"E3.filletArc"),sQuery(id+"F0.wireOp",EDGE,"E4.filletArc"),subQ7,subQ6,subQ5,subQ4,subQ3,subQ2,subQ1,subQ0])],"isStart":true}),makeQuery(id+"F2.opExtrude","CAP_FACE",FACE,{"disambiguationData":[OSD([subQ7,subQ6,subQ5,subQ4,subQ3,subQ2,subQ1,subQ0])],"isStart":true})]});}
            var sketch = newSketch(context, id + "F16", { "sketchPlane" : qUnion([Q0])});
            skPoint(sketch, "E102", {"position": v(-24.7, -24.7) * mm});
            skPoint(sketch, "E103", {"position": v(-12.7, -24.7) * mm});
            skPoint(sketch, "E104", {"position": v(-12.7, -52.3) * mm});
            skPoint(sketch, "E105", {"position": v(-24.7, -52.3) * mm});
            skCircle(sketch, "E106.cCircle", {"center": v(-24.7, -24.7) * mm, "radius": 3.23 * mm, "construction": true});
            skLineSegment(sketch, "E106.0", {"start": v(-21.47, -24.7) * mm, "end": v(-23.08, -27.5) * mm});
            skLineSegment(sketch, "E106.1", {"start": v(-23.08, -27.5) * mm, "end": v(-26.32, -27.5) * mm});
            skLineSegment(sketch, "E106.2", {"start": v(-26.32, -27.5) * mm, "end": v(-27.93, -24.7) * mm});
            skLineSegment(sketch, "E106.3", {"start": v(-27.93, -24.7) * mm, "end": v(-26.32, -21.9) * mm});
            skLineSegment(sketch, "E106.4", {"start": v(-26.32, -21.9) * mm, "end": v(-23.08, -21.9) * mm});
            skLineSegment(sketch, "E106.5", {"start": v(-23.08, -21.9) * mm, "end": v(-21.47, -24.7) * mm});
            skCircle(sketch, "E107.cCircle", {"center": v(-12.7, -24.7) * mm, "radius": 3.23 * mm, "construction": true});
            skLineSegment(sketch, "E107.0", {"start": v(-15.93, -24.7) * mm, "end": v(-14.32, -21.9) * mm});
            skLineSegment(sketch, "E107.1", {"start": v(-14.32, -21.9) * mm, "end": v(-11.08, -21.9) * mm});
            skLineSegment(sketch, "E107.2", {"start": v(-11.08, -21.9) * mm, "end": v(-9.47, -24.7) * mm});
            skLineSegment(sketch, "E107.3", {"start": v(-9.47, -24.7) * mm, "end": v(-11.08, -27.5) * mm});
            skLineSegment(sketch, "E107.4", {"start": v(-11.08, -27.5) * mm, "end": v(-14.32, -27.5) * mm});
            skLineSegment(sketch, "E107.5", {"start": v(-14.32, -27.5) * mm, "end": v(-15.93, -24.7) * mm});
            skCircle(sketch, "E108.cCircle", {"center": v(-12.7, -52.3) * mm, "radius": 3.23 * mm, "construction": true});
            skLineSegment(sketch, "E108.0", {"start": v(-15.93, -52.3) * mm, "end": v(-14.32, -49.5) * mm});
            skLineSegment(sketch, "E108.1", {"start": v(-14.32, -49.5) * mm, "end": v(-11.08, -49.5) * mm});
            skLineSegment(sketch, "E108.2", {"start": v(-11.08, -49.5) * mm, "end": v(-9.47, -52.3) * mm});
            skLineSegment(sketch, "E108.3", {"start": v(-9.47, -52.3) * mm, "end": v(-11.08, -55.1) * mm});
            skLineSegment(sketch, "E108.4", {"start": v(-11.08, -55.1) * mm, "end": v(-14.32, -55.1) * mm});
            skLineSegment(sketch, "E108.5", {"start": v(-14.32, -55.1) * mm, "end": v(-15.93, -52.3) * mm});
            skCircle(sketch, "E109.cCircle", {"center": v(-24.7, -52.3) * mm, "radius": 3.23 * mm, "construction": true});
            skLineSegment(sketch, "E109.0", {"start": v(-21.47, -52.3) * mm, "end": v(-23.08, -55.1) * mm});
            skLineSegment(sketch, "E109.1", {"start": v(-23.08, -55.1) * mm, "end": v(-26.32, -55.1) * mm});
            skLineSegment(sketch, "E109.2", {"start": v(-26.32, -55.1) * mm, "end": v(-27.93, -52.3) * mm});
            skLineSegment(sketch, "E109.3", {"start": v(-27.93, -52.3) * mm, "end": v(-26.32, -49.5) * mm});
            skLineSegment(sketch, "E109.4", {"start": v(-26.32, -49.5) * mm, "end": v(-23.08, -49.5) * mm});
            skLineSegment(sketch, "E109.5", {"start": v(-23.08, -49.5) * mm, "end": v(-21.47, -52.3) * mm});
            skSolve(sketch);
        }
        {
            var Q0;
            Q0=makeQuery(id+"F16.imprint","IMPRINT",FACE,{"disambiguationData":[TD([[makeQuery(id+"F16.imprint","IMPRINT",EDGE,{"derivedFrom":sQuery(id+"F16.wireOp",EDGE,"E107.0")}),-1.0]])]});
            var Q1;
            Q1=makeQuery(id+"F16.imprint","IMPRINT",FACE,{"disambiguationData":[TD([[makeQuery(id+"F16.imprint","IMPRINT",EDGE,{"derivedFrom":sQuery(id+"F16.wireOp",EDGE,"E106.0")}),-1.0]])]});
            var Q2;
            Q2=makeQuery(id+"F16.imprint","IMPRINT",FACE,{"disambiguationData":[TD([[makeQuery(id+"F16.imprint","IMPRINT",EDGE,{"derivedFrom":sQuery(id+"F16.wireOp",EDGE,"E109.0")}),-1.0]])]});
            var Q3;
            Q3=makeQuery(id+"F16.imprint","IMPRINT",FACE,{"disambiguationData":[TD([[makeQuery(id+"F16.imprint","IMPRINT",EDGE,{"derivedFrom":sQuery(id+"F16.wireOp",EDGE,"E108.0")}),-1.0]])]});
            extrude(context, id + "F17", {"entities" : qUnion([Q0, Q1, Q2, Q3]), "operationType" : NewBodyOperationType.REMOVE, "oppositeDirection" : true, "depth" : 2.5 * mm});
        }
        {
            var Q0;
            Q0=makeQuery(id+"F1.opExtrude","CAP_FACE",FACE,{"disambiguationData":[OSD([sQuery(id+"F0.wireOp",EDGE,"E0.bottom"),sQuery(id+"F0.wireOp",EDGE,"E0.top"),sQuery(id+"F0.wireOp",EDGE,"E0.left"),sQuery(id+"F0.wireOp",EDGE,"E0.right"),sQuery(id+"F0.wireOp",EDGE,"E1.filletArc"),sQuery(id+"F0.wireOp",EDGE,"E2.filletArc"),sQuery(id+"F0.wireOp",EDGE,"E3.filletArc"),sQuery(id+"F0.wireOp",EDGE,"E4.filletArc"),sQuery(id+"F0.wireOp",EDGE,"E5.bottom"),sQuery(id+"F0.wireOp",EDGE,"E5.top"),sQuery(id+"F0.wireOp",EDGE,"E5.left"),sQuery(id+"F0.wireOp",EDGE,"E5.right"),sQuery(id+"F0.wireOp",EDGE,"E6.filletArc"),sQuery(id+"F0.wireOp",EDGE,"E7.filletArc"),sQuery(id+"F0.wireOp",EDGE,"E8.filletArc"),sQuery(id+"F0.wireOp",EDGE,"E9.filletArc")])],"isStart":false});
            var sketch = newSketch(context, id + "F18", { "sketchPlane" : qUnion([Q0])});
            skPoint(sketch, "E110", {"position": v(-12.7, 64.3) * mm});
            skPoint(sketch, "E111", {"position": v(-12.7, 12.7) * mm});
            skPoint(sketch, "E112", {"position": v(-59.1, 12.7) * mm});
            skPoint(sketch, "E113", {"position": v(-99.2, 12.7) * mm});
            skPoint(sketch, "E114", {"position": v(-146.8, 12.7) * mm});
            skPoint(sketch, "E115", {"position": v(-146.8, 64.3) * mm});
            skPoint(sketch, "E116", {"position": v(-99.2, 64.3) * mm});
            skPoint(sketch, "E117", {"position": v(-59.1, 64.3) * mm});
            skCircle(sketch, "E118.cCircle", {"center": v(-99.2, 64.3) * mm, "radius": 2.8 * mm, "construction": true});
            skLineSegment(sketch, "E118.0", {"start": v(-96.4, 65.92) * mm, "end": v(-96.4, 62.68) * mm});
            skLineSegment(sketch, "E118.1", {"start": v(-96.4, 62.68) * mm, "end": v(-99.2, 61.07) * mm});
            skLineSegment(sketch, "E118.2", {"start": v(-99.2, 61.07) * mm, "end": v(-102, 62.68) * mm});
            skLineSegment(sketch, "E118.3", {"start": v(-102, 62.68) * mm, "end": v(-102, 65.92) * mm});
            skLineSegment(sketch, "E118.4", {"start": v(-102, 65.92) * mm, "end": v(-99.2, 67.53) * mm});
            skLineSegment(sketch, "E118.5", {"start": v(-99.2, 67.53) * mm, "end": v(-96.4, 65.92) * mm});
            skPoint(sketch, "E118.0.midPoint", {"position": v(-96.4, 64.3) * mm});
            skCircle(sketch, "E119.cCircle", {"center": v(-59.1, 64.3) * mm, "radius": 2.8 * mm, "construction": true});
            skLineSegment(sketch, "E119.0", {"start": v(-61.9, 62.68) * mm, "end": v(-61.9, 65.92) * mm});
            skLineSegment(sketch, "E119.1", {"start": v(-61.9, 65.92) * mm, "end": v(-59.1, 67.53) * mm});
            skLineSegment(sketch, "E119.2", {"start": v(-59.1, 67.53) * mm, "end": v(-56.3, 65.92) * mm});
            skLineSegment(sketch, "E119.3", {"start": v(-56.3, 65.92) * mm, "end": v(-56.3, 62.68) * mm});
            skLineSegment(sketch, "E119.4", {"start": v(-56.3, 62.68) * mm, "end": v(-59.1, 61.07) * mm});
            skLineSegment(sketch, "E119.5", {"start": v(-59.1, 61.07) * mm, "end": v(-61.9, 62.68) * mm});
            skPoint(sketch, "E119.0.midPoint", {"position": v(-61.9, 64.3) * mm});
            skCircle(sketch, "E120.cCircle", {"center": v(-12.7, 64.3) * mm, "radius": 2.8 * mm, "construction": true});
            skLineSegment(sketch, "E120.0", {"start": v(-15.5, 62.68) * mm, "end": v(-15.5, 65.92) * mm});
            skLineSegment(sketch, "E120.1", {"start": v(-15.5, 65.92) * mm, "end": v(-12.7, 67.53) * mm});
            skLineSegment(sketch, "E120.2", {"start": v(-12.7, 67.53) * mm, "end": v(-9.9, 65.92) * mm});
            skLineSegment(sketch, "E120.3", {"start": v(-9.9, 65.92) * mm, "end": v(-9.9, 62.68) * mm});
            skLineSegment(sketch, "E120.4", {"start": v(-9.9, 62.68) * mm, "end": v(-12.7, 61.07) * mm});
            skLineSegment(sketch, "E120.5", {"start": v(-12.7, 61.07) * mm, "end": v(-15.5, 62.68) * mm});
            skPoint(sketch, "E120.0.midPoint", {"position": v(-15.5, 64.3) * mm});
            skCircle(sketch, "E121.cCircle", {"center": v(-146.8, 64.3) * mm, "radius": 2.8 * mm, "construction": true});
            skLineSegment(sketch, "E121.0", {"start": v(-144, 65.92) * mm, "end": v(-144, 62.68) * mm});
            skLineSegment(sketch, "E121.1", {"start": v(-144, 62.68) * mm, "end": v(-146.8, 61.07) * mm});
            skLineSegment(sketch, "E121.2", {"start": v(-146.8, 61.07) * mm, "end": v(-149.6, 62.68) * mm});
            skLineSegment(sketch, "E121.3", {"start": v(-149.6, 62.68) * mm, "end": v(-149.6, 65.92) * mm});
            skLineSegment(sketch, "E121.4", {"start": v(-149.6, 65.92) * mm, "end": v(-146.8, 67.53) * mm});
            skLineSegment(sketch, "E121.5", {"start": v(-146.8, 67.53) * mm, "end": v(-144, 65.92) * mm});
            skPoint(sketch, "E121.0.midPoint", {"position": v(-144, 64.3) * mm});
            skCircle(sketch, "E122.cCircle", {"center": v(-146.8, 12.7) * mm, "radius": 2.8 * mm, "construction": true});
            skLineSegment(sketch, "E122.0", {"start": v(-144, 14.32) * mm, "end": v(-144, 11.08) * mm});
            skLineSegment(sketch, "E122.1", {"start": v(-144, 11.08) * mm, "end": v(-146.8, 9.47) * mm});
            skLineSegment(sketch, "E122.2", {"start": v(-146.8, 9.47) * mm, "end": v(-149.6, 11.08) * mm});
            skLineSegment(sketch, "E122.3", {"start": v(-149.6, 11.08) * mm, "end": v(-149.6, 14.32) * mm});
            skLineSegment(sketch, "E122.4", {"start": v(-149.6, 14.32) * mm, "end": v(-146.8, 15.93) * mm});
            skLineSegment(sketch, "E122.5", {"start": v(-146.8, 15.93) * mm, "end": v(-144, 14.32) * mm});
            skPoint(sketch, "E122.0.midPoint", {"position": v(-144, 12.7) * mm});
            skCircle(sketch, "E123.cCircle", {"center": v(-99.2, 12.7) * mm, "radius": 2.8 * mm, "construction": true});
            skLineSegment(sketch, "E123.0", {"start": v(-96.4, 14.32) * mm, "end": v(-96.4, 11.08) * mm});
            skLineSegment(sketch, "E123.1", {"start": v(-96.4, 11.08) * mm, "end": v(-99.2, 9.47) * mm});
            skLineSegment(sketch, "E123.2", {"start": v(-99.2, 9.47) * mm, "end": v(-102, 11.08) * mm});
            skLineSegment(sketch, "E123.3", {"start": v(-102, 11.08) * mm, "end": v(-102, 14.32) * mm});
            skLineSegment(sketch, "E123.4", {"start": v(-102, 14.32) * mm, "end": v(-99.2, 15.93) * mm});
            skLineSegment(sketch, "E123.5", {"start": v(-99.2, 15.93) * mm, "end": v(-96.4, 14.32) * mm});
            skPoint(sketch, "E123.0.midPoint", {"position": v(-96.4, 12.7) * mm});
            skCircle(sketch, "E124.cCircle", {"center": v(-59.1, 12.7) * mm, "radius": 2.8 * mm, "construction": true});
            skLineSegment(sketch, "E124.0", {"start": v(-61.9, 11.08) * mm, "end": v(-61.9, 14.32) * mm});
            skLineSegment(sketch, "E124.1", {"start": v(-61.9, 14.32) * mm, "end": v(-59.1, 15.93) * mm});
            skLineSegment(sketch, "E124.2", {"start": v(-59.1, 15.93) * mm, "end": v(-56.3, 14.32) * mm});
            skLineSegment(sketch, "E124.3", {"start": v(-56.3, 14.32) * mm, "end": v(-56.3, 11.08) * mm});
            skLineSegment(sketch, "E124.4", {"start": v(-56.3, 11.08) * mm, "end": v(-59.1, 9.47) * mm});
            skLineSegment(sketch, "E124.5", {"start": v(-59.1, 9.47) * mm, "end": v(-61.9, 11.08) * mm});
            skPoint(sketch, "E124.0.midPoint", {"position": v(-61.9, 12.7) * mm});
            skCircle(sketch, "E125.cCircle", {"center": v(-12.7, 12.7) * mm, "radius": 2.8 * mm, "construction": true});
            skLineSegment(sketch, "E125.0", {"start": v(-15.5, 11.08) * mm, "end": v(-15.5, 14.32) * mm});
            skLineSegment(sketch, "E125.1", {"start": v(-15.5, 14.32) * mm, "end": v(-12.7, 15.93) * mm});
            skLineSegment(sketch, "E125.2", {"start": v(-12.7, 15.93) * mm, "end": v(-9.9, 14.32) * mm});
            skLineSegment(sketch, "E125.3", {"start": v(-9.9, 14.32) * mm, "end": v(-9.9, 11.08) * mm});
            skLineSegment(sketch, "E125.4", {"start": v(-9.9, 11.08) * mm, "end": v(-12.7, 9.47) * mm});
            skLineSegment(sketch, "E125.5", {"start": v(-12.7, 9.47) * mm, "end": v(-15.5, 11.08) * mm});
            skPoint(sketch, "E125.0.midPoint", {"position": v(-15.5, 12.7) * mm});
            skLineSegment(sketch, "E126", {"start": v(-59.1, 12.7) * mm, "end": v(-59.1, 64.3) * mm, "construction": true});
            skLineSegment(sketch, "E127", {"start": v(-59.1, 12.7) * mm, "end": v(-99.2, 12.7) * mm, "construction": true});
            skLineSegment(sketch, "E128", {"start": v(-59.1, 12.7) * mm, "end": v(-12.7, 12.7) * mm, "construction": true});
            skLineSegment(sketch, "E129", {"start": v(-59.1, 12.7) * mm, "end": v(-59.1, 0) * mm, "construction": true});
            skLineSegment(sketch, "E130.bottom", {"start": v(-67.25, 12.7) * mm, "end": v(-70.45, 12.7) * mm});
            skLineSegment(sketch, "E131", {"start": v(-68.85, 12.7) * mm, "end": v(-68.85, 17.7) * mm, "construction": true});
            skLineSegment(sketch, "E132", {"start": v(-68.85, 17.7) * mm, "end": v(-68.85, 22.7) * mm, "construction": true});
            skLineSegment(sketch, "E133", {"start": v(-68.85, 22.7) * mm, "end": v(-68.85, 27.7) * mm, "construction": true});
            skLineSegment(sketch, "E134", {"start": v(-68.85, 27.7) * mm, "end": v(-68.85, 32.7) * mm, "construction": true});
            skLineSegment(sketch, "E135", {"start": v(-70.45, 12.7) * mm, "end": v(-70.45, 32.7) * mm});
            skLineSegment(sketch, "E136", {"start": v(-70.45, 32.7) * mm, "end": v(-67.25, 32.7) * mm});
            skLineSegment(sketch, "E137", {"start": v(-67.25, 32.7) * mm, "end": v(-67.25, 12.7) * mm});
            skCircle(sketch, "E138.cCircle", {"center": v(-68.85, 32.7) * mm, "radius": 3.23 * mm, "construction": true});
            skLineSegment(sketch, "E138.0", {"start": v(-65.62, 32.7) * mm, "end": v(-67.23, 29.9) * mm});
            skLineSegment(sketch, "E138.1", {"start": v(-67.23, 29.9) * mm, "end": v(-70.47, 29.9) * mm});
            skLineSegment(sketch, "E138.2", {"start": v(-70.47, 29.9) * mm, "end": v(-72.08, 32.7) * mm});
            skLineSegment(sketch, "E138.3", {"start": v(-72.08, 32.7) * mm, "end": v(-70.47, 35.5) * mm});
            skLineSegment(sketch, "E138.4", {"start": v(-70.47, 35.5) * mm, "end": v(-67.23, 35.5) * mm});
            skLineSegment(sketch, "E138.5", {"start": v(-67.23, 35.5) * mm, "end": v(-65.62, 32.7) * mm});
            skCircle(sketch, "E139.cCircle", {"center": v(-68.85, 27.7) * mm, "radius": 3.23 * mm, "construction": true});
            skLineSegment(sketch, "E139.0", {"start": v(-65.62, 27.7) * mm, "end": v(-67.23, 24.9) * mm});
            skLineSegment(sketch, "E139.1", {"start": v(-67.23, 24.9) * mm, "end": v(-70.47, 24.9) * mm});
            skLineSegment(sketch, "E139.2", {"start": v(-70.47, 24.9) * mm, "end": v(-72.08, 27.7) * mm});
            skLineSegment(sketch, "E139.3", {"start": v(-72.08, 27.7) * mm, "end": v(-70.47, 30.5) * mm});
            skLineSegment(sketch, "E139.5", {"start": v(-67.23, 30.5) * mm, "end": v(-65.62, 27.7) * mm});
            skCircle(sketch, "E140.cCircle", {"center": v(-68.85, 22.7) * mm, "radius": 3.23 * mm, "construction": true});
            skLineSegment(sketch, "E140.0", {"start": v(-65.62, 22.7) * mm, "end": v(-67.23, 19.9) * mm});
            skLineSegment(sketch, "E140.1", {"start": v(-67.23, 19.9) * mm, "end": v(-70.47, 19.9) * mm});
            skLineSegment(sketch, "E140.2", {"start": v(-70.47, 19.9) * mm, "end": v(-72.08, 22.7) * mm});
            skLineSegment(sketch, "E140.3", {"start": v(-72.08, 22.7) * mm, "end": v(-70.47, 25.5) * mm});
            skLineSegment(sketch, "E140.4", {"start": v(-70.47, 25.5) * mm, "end": v(-67.23, 25.5) * mm});
            skLineSegment(sketch, "E140.5", {"start": v(-67.23, 25.5) * mm, "end": v(-65.62, 22.7) * mm});
            skCircle(sketch, "E141.cCircle", {"center": v(-68.85, 17.7) * mm, "radius": 3.23 * mm, "construction": true});
            skLineSegment(sketch, "E141.0", {"start": v(-65.62, 17.7) * mm, "end": v(-67.23, 14.9) * mm});
            skLineSegment(sketch, "E141.1", {"start": v(-67.23, 14.9) * mm, "end": v(-70.47, 14.9) * mm});
            skLineSegment(sketch, "E141.2", {"start": v(-70.47, 14.9) * mm, "end": v(-72.08, 17.7) * mm});
            skLineSegment(sketch, "E141.3", {"start": v(-72.08, 17.7) * mm, "end": v(-70.47, 20.5) * mm});
            skLineSegment(sketch, "E141.4", {"start": v(-70.47, 20.5) * mm, "end": v(-67.23, 20.5) * mm});
            skLineSegment(sketch, "E141.5", {"start": v(-67.23, 20.5) * mm, "end": v(-65.62, 17.7) * mm});
            skCircle(sketch, "E142.cCircle", {"center": v(-68.85, 12.7) * mm, "radius": 3.23 * mm, "construction": true});
            skLineSegment(sketch, "E142.0", {"start": v(-65.62, 12.7) * mm, "end": v(-67.23, 9.9) * mm});
            skLineSegment(sketch, "E142.1", {"start": v(-67.23, 9.9) * mm, "end": v(-70.47, 9.9) * mm});
            skLineSegment(sketch, "E142.2", {"start": v(-70.47, 9.9) * mm, "end": v(-72.08, 12.7) * mm});
            skLineSegment(sketch, "E142.3", {"start": v(-72.08, 12.7) * mm, "end": v(-70.47, 15.5) * mm});
            skLineSegment(sketch, "E142.4", {"start": v(-70.47, 15.5) * mm, "end": v(-67.23, 15.5) * mm});
            skLineSegment(sketch, "E142.5", {"start": v(-67.23, 15.5) * mm, "end": v(-65.62, 12.7) * mm});
            skLineSegment(sketch, "E143", {"start": v(-68.85, 16.77) * mm, "end": v(-59.1, 16.77) * mm, "construction": true});
            skCircle(sketch, "E144", {"center": v(-68.85, 32.7) * mm, "radius": 1.6 * mm});
            skCircle(sketch, "E145", {"center": v(-68.85, 12.7) * mm, "radius": 1.6 * mm});
            skSolve(sketch);
        }
        {
            var Q0;
            Q0=makeQuery(id+"F18.imprint","IMPRINT",FACE,{"disambiguationData":[TD([[makeQuery(id+"F18.imprint","IMPRINT",EDGE,{"derivedFrom":sQuery(id+"F18.wireOp",EDGE,"E120.0")}),-1.0]])]});
            var Q1;
            Q1=makeQuery(id+"F18.imprint","IMPRINT",FACE,{"disambiguationData":[TD([[makeQuery(id+"F18.imprint","IMPRINT",EDGE,{"derivedFrom":sQuery(id+"F18.wireOp",EDGE,"E125.0")}),-1.0]])]});
            var Q2;
            Q2=makeQuery(id+"F18.imprint","IMPRINT",FACE,{"disambiguationData":[TD([[makeQuery(id+"F18.imprint","IMPRINT",EDGE,{"derivedFrom":sQuery(id+"F18.wireOp",EDGE,"E124.0")}),-1.0]])]});
            var Q3;
            Q3=makeQuery(id+"F18.imprint","IMPRINT",FACE,{"disambiguationData":[TD([[makeQuery(id+"F18.imprint","IMPRINT",EDGE,{"derivedFrom":sQuery(id+"F18.wireOp",EDGE,"E119.0")}),-1.0]])]});
            var Q4;
            Q4=makeQuery(id+"F18.imprint","IMPRINT",FACE,{"disambiguationData":[TD([[makeQuery(id+"F18.imprint","IMPRINT",EDGE,{"derivedFrom":sQuery(id+"F18.wireOp",EDGE,"E123.0")}),-1.0]])]});
            var Q5;
            Q5=makeQuery(id+"F18.imprint","IMPRINT",FACE,{"disambiguationData":[TD([[makeQuery(id+"F18.imprint","IMPRINT",EDGE,{"derivedFrom":sQuery(id+"F18.wireOp",EDGE,"E118.0")}),-1.0]])]});
            var Q6;
            Q6=makeQuery(id+"F18.imprint","IMPRINT",FACE,{"disambiguationData":[TD([[makeQuery(id+"F18.imprint","IMPRINT",EDGE,{"derivedFrom":sQuery(id+"F18.wireOp",EDGE,"E122.0")}),-1.0]])]});
            var Q7;
            Q7=makeQuery(id+"F18.imprint","IMPRINT",FACE,{"disambiguationData":[TD([[makeQuery(id+"F18.imprint","IMPRINT",EDGE,{"derivedFrom":sQuery(id+"F18.wireOp",EDGE,"E121.0")}),-1.0]])]});
            var Q8;
            {var subQ1=sQuery(id+"F18.wireOp",EDGE,"E141.1");var subQ5=sQuery(id+"F18.wireOp",EDGE,"E135");var subQ6=makeQuery(id+"F18.imprint","INTERSECT",VERTEX,{"derivedFrom":[subQ5,subQ1]});Q8=makeQuery(id+"F18.imprint","IMPRINT",FACE,{"disambiguationData":[TD([[makeQuery(id+"F18.imprint","IMPRINT",EDGE,{"disambiguationData":[TD([[subQ6,-1.0]])],"derivedFrom":subQ5}),1.0]])]});}
            var Q9;
            {var subQ9=sQuery(id+"F18.wireOp",EDGE,"E135");var subQ11=sQuery(id+"F18.wireOp",EDGE,"E142.4");var subQ12=makeQuery(id+"F18.imprint","INTERSECT",VERTEX,{"derivedFrom":[subQ9,subQ11]});Q9=makeQuery(id+"F18.imprint","IMPRINT",FACE,{"disambiguationData":[TD([[makeQuery(id+"F18.imprint","IMPRINT",EDGE,{"disambiguationData":[TD([[subQ12,-1.0]])],"derivedFrom":subQ9}),1.0]])]});}
            var Q10;
            {var subQ1=sQuery(id+"F18.wireOp",EDGE,"E142.4");var subQ3=sQuery(id+"F18.wireOp",EDGE,"E137");var subQ4=makeQuery(id+"F18.imprint","INTERSECT",VERTEX,{"derivedFrom":[subQ3,subQ1]});Q10=makeQuery(id+"F18.imprint","IMPRINT",FACE,{"disambiguationData":[TD([[makeQuery(id+"F18.imprint","IMPRINT",EDGE,{"disambiguationData":[TD([[subQ4,-1.0]])],"derivedFrom":subQ3}),1.0]])]});}
            var Q11;
            {var subQ0=sQuery(id+"F18.wireOp",EDGE,"E140.1");var subQ3=sQuery(id+"F18.wireOp",EDGE,"E137");var subQ4=makeQuery(id+"F18.imprint","INTERSECT",VERTEX,{"derivedFrom":[subQ3,subQ0]});Q11=makeQuery(id+"F18.imprint","IMPRINT",FACE,{"disambiguationData":[TD([[makeQuery(id+"F18.imprint","IMPRINT",EDGE,{"disambiguationData":[TD([[subQ4,-1.0]])],"derivedFrom":subQ3}),1.0]])]});}
            var Q12;
            {var subQ5=sQuery(id+"F18.wireOp",EDGE,"E139.1");var subQ8=sQuery(id+"F18.wireOp",EDGE,"E137");var subQ9=makeQuery(id+"F18.imprint","INTERSECT",VERTEX,{"derivedFrom":[subQ8,subQ5]});Q12=makeQuery(id+"F18.imprint","IMPRINT",FACE,{"disambiguationData":[TD([[makeQuery(id+"F18.imprint","IMPRINT",EDGE,{"disambiguationData":[TD([[subQ9,-1.0]])],"derivedFrom":subQ8}),1.0]])]});}
            var Q13;
            {var subQ1=sQuery(id+"F18.wireOp",EDGE,"E141.4");var subQ3=sQuery(id+"F18.wireOp",EDGE,"E137");var subQ4=makeQuery(id+"F18.imprint","INTERSECT",VERTEX,{"derivedFrom":[subQ3,subQ1]});Q13=makeQuery(id+"F18.imprint","IMPRINT",FACE,{"disambiguationData":[TD([[makeQuery(id+"F18.imprint","IMPRINT",EDGE,{"disambiguationData":[TD([[subQ4,-1.0]])],"derivedFrom":subQ3}),1.0]])]});}
            var Q14;
            {var subQ5=sQuery(id+"F18.wireOp",EDGE,"E140.1");var subQ7=sQuery(id+"F18.wireOp",EDGE,"E135");var subQ9=makeQuery(id+"F18.imprint","INTERSECT",VERTEX,{"derivedFrom":[subQ7,subQ5]});Q14=makeQuery(id+"F18.imprint","IMPRINT",FACE,{"disambiguationData":[TD([[makeQuery(id+"F18.imprint","IMPRINT",EDGE,{"disambiguationData":[TD([[subQ9,-1.0]])],"derivedFrom":subQ7}),1.0]])]});}
            var Q15;
            {var subQ9=sQuery(id+"F18.wireOp",EDGE,"E135");var subQ11=sQuery(id+"F18.wireOp",EDGE,"E141.4");var subQ12=makeQuery(id+"F18.imprint","INTERSECT",VERTEX,{"derivedFrom":[subQ9,subQ11]});Q15=makeQuery(id+"F18.imprint","IMPRINT",FACE,{"disambiguationData":[TD([[makeQuery(id+"F18.imprint","IMPRINT",EDGE,{"disambiguationData":[TD([[subQ12,-1.0]])],"derivedFrom":subQ9}),1.0]])]});}
            var Q16;
            {var subQ5=sQuery(id+"F18.wireOp",EDGE,"E139.1");var subQ7=sQuery(id+"F18.wireOp",EDGE,"E135");var subQ8=makeQuery(id+"F18.imprint","INTERSECT",VERTEX,{"derivedFrom":[subQ7,subQ5]});Q16=makeQuery(id+"F18.imprint","IMPRINT",FACE,{"disambiguationData":[TD([[makeQuery(id+"F18.imprint","IMPRINT",EDGE,{"disambiguationData":[TD([[subQ8,-1.0]])],"derivedFrom":subQ7}),1.0]])]});}
            var Q17;
            {var subQ1=sQuery(id+"F18.wireOp",EDGE,"E140.4");var subQ3=sQuery(id+"F18.wireOp",EDGE,"E137");var subQ4=makeQuery(id+"F18.imprint","INTERSECT",VERTEX,{"derivedFrom":[subQ3,subQ1]});Q17=makeQuery(id+"F18.imprint","IMPRINT",FACE,{"disambiguationData":[TD([[makeQuery(id+"F18.imprint","IMPRINT",EDGE,{"disambiguationData":[TD([[subQ4,-1.0]])],"derivedFrom":subQ3}),1.0]])]});}
            var Q18;
            {var subQ5=sQuery(id+"F18.wireOp",EDGE,"E138.1");var subQ8=sQuery(id+"F18.wireOp",EDGE,"E137");var subQ9=makeQuery(id+"F18.imprint","INTERSECT",VERTEX,{"derivedFrom":[subQ8,subQ5]});Q18=makeQuery(id+"F18.imprint","IMPRINT",FACE,{"disambiguationData":[TD([[makeQuery(id+"F18.imprint","IMPRINT",EDGE,{"disambiguationData":[TD([[subQ9,-1.0]])],"derivedFrom":subQ8}),1.0]])]});}
            var Q19;
            {var subQ5=sQuery(id+"F18.wireOp",EDGE,"E135");var subQ11=sQuery(id+"F18.wireOp",EDGE,"E140.4");var subQ13=makeQuery(id+"F18.imprint","INTERSECT",VERTEX,{"derivedFrom":[subQ5,subQ11]});Q19=makeQuery(id+"F18.imprint","IMPRINT",FACE,{"disambiguationData":[TD([[makeQuery(id+"F18.imprint","IMPRINT",EDGE,{"disambiguationData":[TD([[subQ13,-1.0]])],"derivedFrom":subQ5}),1.0]])]});}
            var Q20;
            {var subQ6=sQuery(id+"F18.wireOp",EDGE,"E138.3");Q20=makeQuery(id+"F18.imprint","IMPRINT",FACE,{"disambiguationData":[TD([[makeQuery(id+"F18.imprint","IMPRINT",EDGE,{"derivedFrom":subQ6}),-1.0]])]});}
            var Q21;
            {var subQ16=sQuery(id+"F18.wireOp",EDGE,"E142.0");Q21=makeQuery(id+"F18.imprint","IMPRINT",FACE,{"disambiguationData":[TD([[makeQuery(id+"F18.imprint","IMPRINT",EDGE,{"derivedFrom":subQ16}),-1.0]])]});}
            extrude(context, id + "F19", {"entities" : qUnion([Q0, Q1, Q2, Q3, Q4, Q5, Q6, Q7, Q8, Q9, Q10, Q11, Q12, Q13, Q14, Q15, Q16, Q17, Q18, Q19, Q20, Q21]), "operationType" : NewBodyOperationType.REMOVE, "oppositeDirection" : true, "depth" : 2.5 * mm});
        }
        {
            var Q0;
            Q0=makeQuery(id+"F1.opExtrude","CAP_EDGE",EDGE,{"disambiguationData":[OSD([sQuery(id+"F0.wireOp",EDGE,"E0.bottom")])],"isStart":true});
            fillet(context, id + "F20", {"entities" : qUnion([Q0]), "radius" : 1 * mm, "tangentPropagation" : true, "allowEdgeOverflow" : false});
        }
        {
            var Q0;
            Q0=makeQuery(id+"F1.opExtrude","CAP_FACE",FACE,{"disambiguationData":[OSD([sQuery(id+"F0.wireOp",EDGE,"E0.bottom"),sQuery(id+"F0.wireOp",EDGE,"E0.top"),sQuery(id+"F0.wireOp",EDGE,"E0.left"),sQuery(id+"F0.wireOp",EDGE,"E0.right"),sQuery(id+"F0.wireOp",EDGE,"E1.filletArc"),sQuery(id+"F0.wireOp",EDGE,"E2.filletArc"),sQuery(id+"F0.wireOp",EDGE,"E3.filletArc"),sQuery(id+"F0.wireOp",EDGE,"E4.filletArc"),sQuery(id+"F0.wireOp",EDGE,"E5.bottom"),sQuery(id+"F0.wireOp",EDGE,"E5.top"),sQuery(id+"F0.wireOp",EDGE,"E5.left"),sQuery(id+"F0.wireOp",EDGE,"E5.right"),sQuery(id+"F0.wireOp",EDGE,"E6.filletArc"),sQuery(id+"F0.wireOp",EDGE,"E7.filletArc"),sQuery(id+"F0.wireOp",EDGE,"E8.filletArc"),sQuery(id+"F0.wireOp",EDGE,"E9.filletArc")])],"isStart":false});
            var sketch = newSketch(context, id + "F21", { "sketchPlane" : qUnion([Q0])});
            skLineSegment(sketch, "E146", {"start": v(0, 57.3) * mm, "end": v(-16.6, 57.3) * mm});
            skLineSegment(sketch, "E147", {"start": v(-16.6, 57.3) * mm, "end": v(-16.6, 19.7) * mm});
            skLineSegment(sketch, "E148", {"start": v(-16.6, 19.7) * mm, "end": v(0, 19.7) * mm});
            skLineSegment(sketch, "E149", {"start": v(0, 19.7) * mm, "end": v(0, 57.3) * mm});
            skSolve(sketch);
        }
        {
            var Q0;
            {var subQ4=sQuery(id+"F21.wireOp",EDGE,"E146");Q0=makeQuery(id+"F21.imprint","IMPRINT",FACE,{"disambiguationData":[TD([[makeQuery(id+"F21.imprint","IMPRINT",EDGE,{"derivedFrom":subQ4}),1.0]])]});}
            extrude(context, id + "F22", {"entities" : qUnion([Q0]), "operationType" : NewBodyOperationType.REMOVE, "oppositeDirection" : true, "depth" : 2.5 * mm});
        }
        {
            var Q0;
            Q0=makeQuery(id+"F1.opExtrude","CAP_EDGE",EDGE,{"disambiguationData":[OSD([sQuery(id+"F0.wireOp",EDGE,"E0.bottom")])],"isStart":false});
            fillet(context, id + "F23", {"entities" : qUnion([Q0]), "radius" : 2 * mm, "tangentPropagation" : true, "allowEdgeOverflow" : false});
        }
        {
            var Q0;
            {var subQ0=sQuery(id+"F18.wireOp",EDGE,"E136");Q0=makeQuery(id+"F18.imprint","IMPRINT",FACE,{"disambiguationData":[TD([[makeQuery(id+"F18.imprint","IMPRINT",EDGE,{"derivedFrom":subQ0}),-1.0]])]});}
            var Q1;
            {var subQ0=sQuery(id+"F18.wireOp",EDGE,"E140.4");var subQ1=sQuery(id+"F18.wireOp",EDGE,"E135");var subQ2=makeQuery(id+"F18.imprint","INTERSECT",VERTEX,{"derivedFrom":[subQ1,subQ0]});Q1=makeQuery(id+"F18.imprint","IMPRINT",FACE,{"disambiguationData":[TD([[makeQuery(id+"F18.imprint","IMPRINT",EDGE,{"disambiguationData":[TD([[subQ2,-1.0]])],"derivedFrom":subQ1}),-1.0]])]});}
            var Q2;
            {var subQ0=sQuery(id+"F18.wireOp",EDGE,"E139.1");var subQ1=sQuery(id+"F18.wireOp",EDGE,"E135");var subQ2=makeQuery(id+"F18.imprint","INTERSECT",VERTEX,{"derivedFrom":[subQ1,subQ0]});Q2=makeQuery(id+"F18.imprint","IMPRINT",FACE,{"disambiguationData":[TD([[makeQuery(id+"F18.imprint","IMPRINT",EDGE,{"disambiguationData":[TD([[subQ2,-1.0]])],"derivedFrom":subQ1}),-1.0]])]});}
            var Q3;
            {var subQ0=sQuery(id+"F18.wireOp",EDGE,"E141.4");var subQ1=sQuery(id+"F18.wireOp",EDGE,"E135");var subQ2=makeQuery(id+"F18.imprint","INTERSECT",VERTEX,{"derivedFrom":[subQ1,subQ0]});Q3=makeQuery(id+"F18.imprint","IMPRINT",FACE,{"disambiguationData":[TD([[makeQuery(id+"F18.imprint","IMPRINT",EDGE,{"disambiguationData":[TD([[subQ2,-1.0]])],"derivedFrom":subQ1}),-1.0]])]});}
            var Q4;
            {var subQ0=sQuery(id+"F18.wireOp",EDGE,"E130.bottom");Q4=makeQuery(id+"F18.imprint","IMPRINT",FACE,{"disambiguationData":[TD([[makeQuery(id+"F18.imprint","IMPRINT",EDGE,{"derivedFrom":subQ0}),-1.0]])]});}
            var Q5;
            {var subQ0=sQuery(id+"F18.wireOp",EDGE,"E142.4");var subQ1=sQuery(id+"F18.wireOp",EDGE,"E135");var subQ2=makeQuery(id+"F18.imprint","INTERSECT",VERTEX,{"derivedFrom":[subQ1,subQ0]});Q5=makeQuery(id+"F18.imprint","IMPRINT",FACE,{"disambiguationData":[TD([[makeQuery(id+"F18.imprint","IMPRINT",EDGE,{"disambiguationData":[TD([[subQ2,-1.0]])],"derivedFrom":subQ1}),-1.0]])]});}
            var Q6;
            {var subQ0=sQuery(id+"F18.wireOp",EDGE,"E140.1");var subQ1=sQuery(id+"F18.wireOp",EDGE,"E135");var subQ2=makeQuery(id+"F18.imprint","INTERSECT",VERTEX,{"derivedFrom":[subQ1,subQ0]});Q6=makeQuery(id+"F18.imprint","IMPRINT",FACE,{"disambiguationData":[TD([[makeQuery(id+"F18.imprint","IMPRINT",EDGE,{"disambiguationData":[TD([[subQ2,-1.0]])],"derivedFrom":subQ1}),-1.0]])]});}
            var Q7;
            {var subQ0=sQuery(id+"F18.wireOp",EDGE,"E141.1");var subQ1=sQuery(id+"F18.wireOp",EDGE,"E135");var subQ2=makeQuery(id+"F18.imprint","INTERSECT",VERTEX,{"derivedFrom":[subQ1,subQ0]});Q7=makeQuery(id+"F18.imprint","IMPRINT",FACE,{"disambiguationData":[TD([[makeQuery(id+"F18.imprint","IMPRINT",EDGE,{"disambiguationData":[TD([[subQ2,-1.0]])],"derivedFrom":subQ1}),-1.0]])]});}
            var Q8;
            {var subQ2=sQuery(id+"F18.wireOp",EDGE,"E135");var subQ4=sQuery(id+"F18.wireOp",EDGE,"E138.1");var subQ5=makeQuery(id+"F18.imprint","INTERSECT",VERTEX,{"derivedFrom":[subQ2,subQ4]});Q8=makeQuery(id+"F18.imprint","IMPRINT",FACE,{"disambiguationData":[TD([[makeQuery(id+"F18.imprint","IMPRINT",EDGE,{"disambiguationData":[TD([[subQ5,1.0]])],"derivedFrom":subQ4}),-1.0]])]});}
            var Q9;
            {var subQ1=sQuery(id+"F18.wireOp",EDGE,"E135");var subQ4=sQuery(id+"F18.wireOp",EDGE,"E141.1");var subQ5=makeQuery(id+"F18.imprint","INTERSECT",VERTEX,{"derivedFrom":[subQ1,subQ4]});Q9=makeQuery(id+"F18.imprint","IMPRINT",FACE,{"disambiguationData":[TD([[makeQuery(id+"F18.imprint","IMPRINT",EDGE,{"disambiguationData":[TD([[subQ5,1.0]])],"derivedFrom":subQ4}),1.0]])]});}
            var Q10;
            {var subQ0=sQuery(id+"F18.wireOp",EDGE,"E130.bottom");Q10=makeQuery(id+"F18.imprint","IMPRINT",FACE,{"disambiguationData":[TD([[makeQuery(id+"F18.imprint","IMPRINT",EDGE,{"derivedFrom":subQ0}),1.0]])]});}
            var Q11;
            {var subQ0=sQuery(id+"F18.wireOp",EDGE,"E136");Q11=makeQuery(id+"F18.imprint","IMPRINT",FACE,{"disambiguationData":[TD([[makeQuery(id+"F18.imprint","IMPRINT",EDGE,{"derivedFrom":subQ0}),1.0]])]});}
            extrude(context, id + "F24", {"entities" : qUnion([Q0, Q1, Q2, Q3, Q4, Q5, Q6, Q7, Q8, Q9, Q10, Q11]), "operationType" : NewBodyOperationType.REMOVE, "oppositeDirection" : true, "depth" : 25 * mm});
        }
    });
